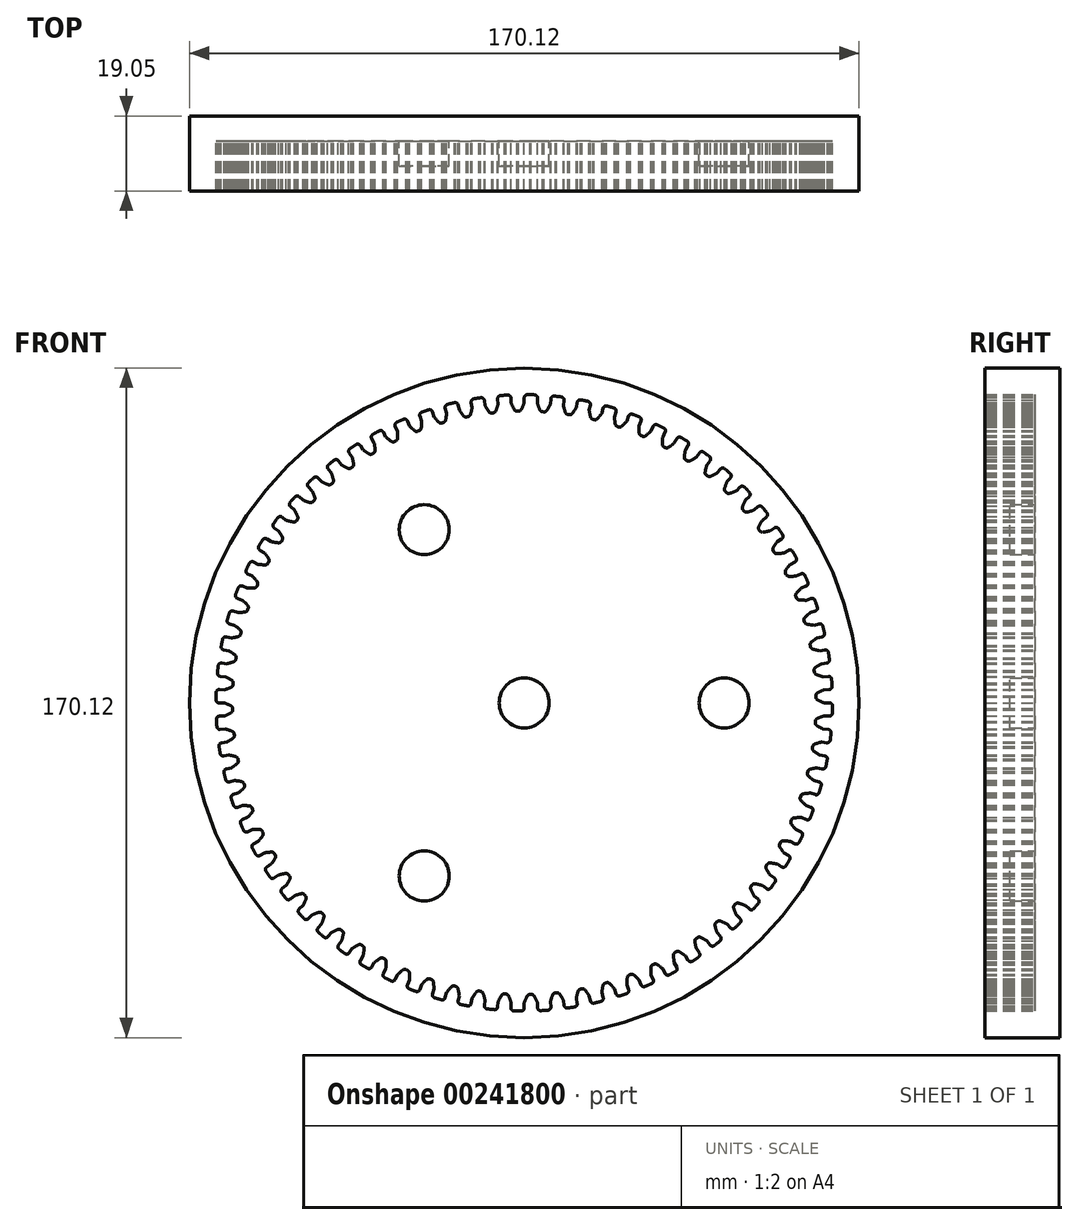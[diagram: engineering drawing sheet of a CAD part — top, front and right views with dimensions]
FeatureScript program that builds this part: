
annotation { "Feature Type Name" : "Feature", "Feature Type Description" : "" }
export const myFeature = defineFeature(function(context is Context, id is Id, definition is map)
    precondition{}
    {
        {
            var Q0;
            Q0=qCreatedBy(makeId("Front.planeOp"),FACE);
            var sketch = newSketch(context, id + "F0", { "sketchPlane" : qUnion([Q0])});
            skArc(sketch, "E0", {"start": v(-4.21, 78.2) * mm, "mid": v(-5.12, 78.15) * mm, "end": v(-6.03, 78.08) * mm});
            skLineSegment(sketch, "E1.MirrorCS", {"start": v(0, 76.2) * mm, "end": v(0, 77.53) * mm});
            skArc(sketch, "E2.MirrorCS", {"start": v(0, 76.2) * mm, "mid": v(-0.35, 75.36) * mm, "end": v(-0.73, 74.54) * mm});
            skArc(sketch, "E3.MirrorCS", {"start": v(-3.32, 76.13) * mm, "mid": v(-2.94, 75.3) * mm, "end": v(-2.52, 74.5) * mm});
            skLineSegment(sketch, "E4.MirrorCS", {"start": v(-3.32, 76.13) * mm, "end": v(-3.38, 77.45) * mm});
            skPoint(sketch, "E5.visualSharp", {"position": v(-2.27, 74.06) * mm});
            skArc(sketch, "E5.filletArc", {"start": v(-2.52, 74.5) * mm, "mid": v(-2.2, 74.19) * mm, "end": v(-1.78, 74.1) * mm});
            skPoint(sketch, "E6.visualSharp", {"position": v(-0.96, 74.09) * mm});
            skArc(sketch, "E6.filletArc", {"start": v(-1.45, 74.1) * mm, "mid": v(-1.03, 74.21) * mm, "end": v(-0.73, 74.54) * mm});
            skLineSegment(sketch, "E7", {"start": v(-1.78, 74.1) * mm, "end": v(-1.45, 74.1) * mm});
            skCircle(sketch, "E8", {"center": v(0, 0) * mm, "radius": 85.06 * mm});
            skPoint(sketch, "E9.visualSharp", {"position": v(-3.42, 78.24) * mm});
            skPoint(sketch, "E10.visualSharp", {"position": v(0, 78.32) * mm});
            skArc(sketch, "E11.filletArc", {"start": v(0.8, 78.31) * mm, "mid": v(0.23, 78.08) * mm, "end": v(0, 77.53) * mm});
            skArc(sketch, "E12.filletArc", {"start": v(-3.38, 77.45) * mm, "mid": v(-3.64, 78) * mm, "end": v(-4.21, 78.2) * mm});
            skArc(sketch, "E13.1.0", {"start": v(-10.12, 76.86) * mm, "mid": v(-10.42, 77.39) * mm, "end": v(-11.01, 77.54) * mm});
            skLineSegment(sketch, "E13.1.1", {"start": v(-9.95, 75.55) * mm, "end": v(-10.12, 76.86) * mm});
            skArc(sketch, "E13.1.2", {"start": v(-9.95, 75.55) * mm, "mid": v(-9.5, 74.76) * mm, "end": v(-9, 74) * mm});
            skArc(sketch, "E13.1.3", {"start": v(-9, 74) * mm, "mid": v(-8.66, 73.71) * mm, "end": v(-8.23, 73.66) * mm});
            skLineSegment(sketch, "E13.1.4", {"start": v(-8.23, 73.66) * mm, "end": v(-7.9, 73.7) * mm});
            skArc(sketch, "E13.1.5", {"start": v(-7.9, 73.7) * mm, "mid": v(-7.5, 73.84) * mm, "end": v(-7.23, 74.19) * mm});
            skArc(sketch, "E13.1.6", {"start": v(-6.64, 75.91) * mm, "mid": v(-6.91, 75.04) * mm, "end": v(-7.23, 74.19) * mm});
            skLineSegment(sketch, "E13.1.7", {"start": v(-6.64, 75.91) * mm, "end": v(-6.76, 77.23) * mm});
            skArc(sketch, "E13.1.8", {"start": v(-6.03, 78.08) * mm, "mid": v(-6.57, 77.8) * mm, "end": v(-6.76, 77.23) * mm});
            skArc(sketch, "E13.2.0", {"start": v(-16.78, 75.69) * mm, "mid": v(-17.13, 76.18) * mm, "end": v(-17.73, 76.28) * mm});
            skLineSegment(sketch, "E13.2.1", {"start": v(-16.5, 74.4) * mm, "end": v(-16.78, 75.69) * mm});
            skArc(sketch, "E13.2.2", {"start": v(-16.5, 74.4) * mm, "mid": v(-15.97, 73.65) * mm, "end": v(-15.42, 72.93) * mm});
            skArc(sketch, "E13.2.3", {"start": v(-15.42, 72.93) * mm, "mid": v(-15.06, 72.68) * mm, "end": v(-14.62, 72.66) * mm});
            skLineSegment(sketch, "E13.2.4", {"start": v(-14.62, 72.66) * mm, "end": v(-14.3, 72.72) * mm});
            skArc(sketch, "E13.2.5", {"start": v(-14.3, 72.72) * mm, "mid": v(-13.9, 72.9) * mm, "end": v(-13.66, 73.28) * mm});
            skArc(sketch, "E13.2.6", {"start": v(-13.23, 75.04) * mm, "mid": v(-13.43, 74.15) * mm, "end": v(-13.66, 73.28) * mm});
            skLineSegment(sketch, "E13.2.7", {"start": v(-13.23, 75.04) * mm, "end": v(-13.46, 76.35) * mm});
            skArc(sketch, "E13.2.8", {"start": v(-12.82, 77.26) * mm, "mid": v(-13.33, 76.94) * mm, "end": v(-13.46, 76.35) * mm});
            skArc(sketch, "E14.1.3.0", {"start": v(-23.31, 73.94) * mm, "mid": v(-23.7, 74.4) * mm, "end": v(-24.3, 74.45) * mm});
            skLineSegment(sketch, "E14.4.3.0", {"start": v(-22.91, 72.67) * mm, "end": v(-23.31, 73.94) * mm});
            skArc(sketch, "E14.7.3.0", {"start": v(-22.91, 72.67) * mm, "mid": v(-22.33, 71.98) * mm, "end": v(-21.71, 71.3) * mm});
            skArc(sketch, "E14.11.3.0", {"start": v(-21.71, 71.3) * mm, "mid": v(-21.33, 71.09) * mm, "end": v(-20.9, 71.1) * mm});
            skLineSegment(sketch, "E14.15.3.0", {"start": v(-20.9, 71.1) * mm, "end": v(-20.58, 71.2) * mm});
            skArc(sketch, "E14.18.3.0", {"start": v(-20.58, 71.2) * mm, "mid": v(-20.2, 71.42) * mm, "end": v(-20, 71.8) * mm});
            skArc(sketch, "E14.22.3.0", {"start": v(-19.72, 73.6) * mm, "mid": v(-19.84, 72.7) * mm, "end": v(-20, 71.8) * mm});
            skLineSegment(sketch, "E14.26.3.0", {"start": v(-19.72, 73.6) * mm, "end": v(-20.07, 74.88) * mm});
            skArc(sketch, "E14.29.3.0", {"start": v(-19.5, 75.85) * mm, "mid": v(-19.98, 75.48) * mm, "end": v(-20.07, 74.88) * mm});
            skArc(sketch, "E14.1.4.0", {"start": v(-29.67, 71.62) * mm, "mid": v(-30.1, 72.05) * mm, "end": v(-30.7, 72.05) * mm});
            skLineSegment(sketch, "E14.4.4.0", {"start": v(-29.16, 70.4) * mm, "end": v(-29.67, 71.62) * mm});
            skArc(sketch, "E14.7.4.0", {"start": v(-29.16, 70.4) * mm, "mid": v(-28.52, 69.76) * mm, "end": v(-27.85, 69.14) * mm});
            skArc(sketch, "E14.11.4.0", {"start": v(-27.85, 69.14) * mm, "mid": v(-27.45, 68.96) * mm, "end": v(-27.01, 69.02) * mm});
            skLineSegment(sketch, "E14.15.4.0", {"start": v(-27.01, 69.02) * mm, "end": v(-26.71, 69.13) * mm});
            skArc(sketch, "E14.18.4.0", {"start": v(-26.71, 69.13) * mm, "mid": v(-26.35, 69.39) * mm, "end": v(-26.18, 69.79) * mm});
            skArc(sketch, "E14.22.4.0", {"start": v(-26.06, 71.6) * mm, "mid": v(-26.1, 70.7) * mm, "end": v(-26.18, 69.79) * mm});
            skLineSegment(sketch, "E14.26.4.0", {"start": v(-26.06, 71.6) * mm, "end": v(-26.52, 72.85) * mm});
            skArc(sketch, "E14.29.4.0", {"start": v(-26.04, 73.86) * mm, "mid": v(-26.49, 73.46) * mm, "end": v(-26.52, 72.85) * mm});
            skArc(sketch, "E14.1.5.0", {"start": v(-35.8, 68.77) * mm, "mid": v(-36.26, 69.15) * mm, "end": v(-36.87, 69.1) * mm});
            skLineSegment(sketch, "E14.4.5.0", {"start": v(-35.19, 67.6) * mm, "end": v(-35.8, 68.77) * mm});
            skArc(sketch, "E14.7.5.0", {"start": v(-35.19, 67.6) * mm, "mid": v(-34.49, 67) * mm, "end": v(-33.77, 66.45) * mm});
            skArc(sketch, "E14.11.5.0", {"start": v(-33.77, 66.45) * mm, "mid": v(-33.35, 66.3) * mm, "end": v(-32.93, 66.4) * mm});
            skLineSegment(sketch, "E14.15.5.0", {"start": v(-32.93, 66.4) * mm, "end": v(-32.63, 66.54) * mm});
            skArc(sketch, "E14.18.5.0", {"start": v(-32.63, 66.54) * mm, "mid": v(-32.3, 66.82) * mm, "end": v(-32.16, 67.24) * mm});
            skArc(sketch, "E14.22.5.0", {"start": v(-32.2, 69.06) * mm, "mid": v(-32.16, 68.15) * mm, "end": v(-32.16, 67.24) * mm});
            skLineSegment(sketch, "E14.26.5.0", {"start": v(-32.2, 69.06) * mm, "end": v(-32.76, 70.26) * mm});
            skArc(sketch, "E14.29.5.0", {"start": v(-32.38, 71.31) * mm, "mid": v(-32.79, 70.87) * mm, "end": v(-32.76, 70.26) * mm});
            skArc(sketch, "E14.1.6.0", {"start": v(-41.65, 65.38) * mm, "mid": v(-42.15, 65.73) * mm, "end": v(-42.75, 65.62) * mm});
            skLineSegment(sketch, "E14.4.6.0", {"start": v(-40.94, 64.27) * mm, "end": v(-41.65, 65.38) * mm});
            skArc(sketch, "E14.7.6.0", {"start": v(-40.94, 64.27) * mm, "mid": v(-40.2, 63.74) * mm, "end": v(-39.43, 63.26) * mm});
            skArc(sketch, "E14.11.6.0", {"start": v(-39.43, 63.26) * mm, "mid": v(-39, 63.14) * mm, "end": v(-38.59, 63.28) * mm});
            skLineSegment(sketch, "E14.15.6.0", {"start": v(-38.59, 63.28) * mm, "end": v(-38.3, 63.45) * mm});
            skArc(sketch, "E14.18.6.0", {"start": v(-38.3, 63.45) * mm, "mid": v(-38, 63.76) * mm, "end": v(-37.9, 64.18) * mm});
            skArc(sketch, "E14.22.6.0", {"start": v(-38.1, 66) * mm, "mid": v(-37.98, 65.09) * mm, "end": v(-37.9, 64.18) * mm});
            skLineSegment(sketch, "E14.26.6.0", {"start": v(-38.1, 66) * mm, "end": v(-38.76, 67.14) * mm});
            skArc(sketch, "E14.29.6.0", {"start": v(-38.47, 68.22) * mm, "mid": v(-38.84, 67.74) * mm, "end": v(-38.76, 67.14) * mm});
            skArc(sketch, "E14.1.7.0", {"start": v(-47.2, 61.5) * mm, "mid": v(-47.72, 61.8) * mm, "end": v(-48.3, 61.65) * mm});
            skLineSegment(sketch, "E14.4.7.0", {"start": v(-46.39, 60.45) * mm, "end": v(-47.2, 61.5) * mm});
            skArc(sketch, "E14.7.7.0", {"start": v(-46.39, 60.45) * mm, "mid": v(-45.6, 60) * mm, "end": v(-44.8, 59.58) * mm});
            skArc(sketch, "E14.11.7.0", {"start": v(-44.8, 59.58) * mm, "mid": v(-44.36, 59.5) * mm, "end": v(-43.96, 59.67) * mm});
            skLineSegment(sketch, "E14.15.7.0", {"start": v(-43.96, 59.67) * mm, "end": v(-43.7, 59.86) * mm});
            skArc(sketch, "E14.18.7.0", {"start": v(-43.7, 59.86) * mm, "mid": v(-43.41, 60.2) * mm, "end": v(-43.35, 60.64) * mm});
            skArc(sketch, "E14.22.7.0", {"start": v(-43.7, 62.42) * mm, "mid": v(-43.5, 61.53) * mm, "end": v(-43.35, 60.64) * mm});
            skLineSegment(sketch, "E14.26.7.0", {"start": v(-43.7, 62.42) * mm, "end": v(-44.47, 63.5) * mm});
            skArc(sketch, "E14.29.7.0", {"start": v(-44.27, 64.6) * mm, "mid": v(-44.6, 64.1) * mm, "end": v(-44.47, 63.5) * mm});
            skArc(sketch, "E14.1.8.0", {"start": v(-52.38, 57.16) * mm, "mid": v(-52.93, 57.41) * mm, "end": v(-53.5, 57.2) * mm});
            skLineSegment(sketch, "E14.4.8.0", {"start": v(-51.48, 56.18) * mm, "end": v(-52.38, 57.16) * mm});
            skArc(sketch, "E14.7.8.0", {"start": v(-51.48, 56.18) * mm, "mid": v(-50.66, 55.8) * mm, "end": v(-49.82, 55.45) * mm});
            skArc(sketch, "E14.11.8.0", {"start": v(-49.82, 55.45) * mm, "mid": v(-49.38, 55.41) * mm, "end": v(-48.99, 55.62) * mm});
            skLineSegment(sketch, "E14.15.8.0", {"start": v(-48.99, 55.62) * mm, "end": v(-48.75, 55.83) * mm});
            skArc(sketch, "E14.18.8.0", {"start": v(-48.75, 55.83) * mm, "mid": v(-48.5, 56.19) * mm, "end": v(-48.47, 56.63) * mm});
            skArc(sketch, "E14.22.8.0", {"start": v(-48.98, 58.37) * mm, "mid": v(-48.7, 57.5) * mm, "end": v(-48.47, 56.63) * mm});
            skLineSegment(sketch, "E14.26.8.0", {"start": v(-48.98, 58.37) * mm, "end": v(-49.83, 59.39) * mm});
            skArc(sketch, "E14.29.8.0", {"start": v(-49.73, 60.5) * mm, "mid": v(-50.01, 59.97) * mm, "end": v(-49.83, 59.39) * mm});
            skArc(sketch, "E14.1.9.0", {"start": v(-57.16, 52.38) * mm, "mid": v(-57.73, 52.58) * mm, "end": v(-58.28, 52.32) * mm});
            skLineSegment(sketch, "E14.4.9.0", {"start": v(-56.18, 51.48) * mm, "end": v(-57.16, 52.38) * mm});
            skArc(sketch, "E14.7.9.0", {"start": v(-56.18, 51.48) * mm, "mid": v(-55.33, 51.17) * mm, "end": v(-54.46, 50.9) * mm});
            skArc(sketch, "E14.11.9.0", {"start": v(-54.46, 50.9) * mm, "mid": v(-54.02, 50.9) * mm, "end": v(-53.65, 51.13) * mm});
            skLineSegment(sketch, "E14.15.9.0", {"start": v(-53.65, 51.13) * mm, "end": v(-53.43, 51.37) * mm});
            skArc(sketch, "E14.18.9.0", {"start": v(-53.43, 51.37) * mm, "mid": v(-53.2, 51.75) * mm, "end": v(-53.22, 52.19) * mm});
            skArc(sketch, "E14.22.9.0", {"start": v(-53.88, 53.88) * mm, "mid": v(-53.53, 53.04) * mm, "end": v(-53.22, 52.19) * mm});
            skLineSegment(sketch, "E14.26.9.0", {"start": v(-53.88, 53.88) * mm, "end": v(-54.82, 54.82) * mm});
            skArc(sketch, "E14.29.9.0", {"start": v(-54.81, 55.94) * mm, "mid": v(-55.05, 55.38) * mm, "end": v(-54.82, 54.82) * mm});
            skArc(sketch, "E14.1.10.0", {"start": v(-61.5, 47.2) * mm, "mid": v(-62.1, 47.35) * mm, "end": v(-62.61, 47.04) * mm});
            skLineSegment(sketch, "E14.4.10.0", {"start": v(-60.45, 46.39) * mm, "end": v(-61.5, 47.2) * mm});
            skArc(sketch, "E14.7.10.0", {"start": v(-60.45, 46.39) * mm, "mid": v(-59.58, 46.15) * mm, "end": v(-58.69, 45.96) * mm});
            skArc(sketch, "E14.11.10.0", {"start": v(-58.69, 45.96) * mm, "mid": v(-58.25, 46) * mm, "end": v(-57.9, 46.26) * mm});
            skLineSegment(sketch, "E14.15.10.0", {"start": v(-57.9, 46.26) * mm, "end": v(-57.7, 46.52) * mm});
            skArc(sketch, "E14.18.10.0", {"start": v(-57.7, 46.52) * mm, "mid": v(-57.51, 46.91) * mm, "end": v(-57.57, 47.35) * mm});
            skArc(sketch, "E14.22.10.0", {"start": v(-58.37, 48.98) * mm, "mid": v(-57.95, 48.17) * mm, "end": v(-57.57, 47.35) * mm});
            skLineSegment(sketch, "E14.26.10.0", {"start": v(-58.37, 48.98) * mm, "end": v(-59.39, 49.83) * mm});
            skArc(sketch, "E14.29.10.0", {"start": v(-59.48, 50.95) * mm, "mid": v(-59.67, 50.37) * mm, "end": v(-59.39, 49.83) * mm});
            skArc(sketch, "E14.1.11.0", {"start": v(-65.38, 41.65) * mm, "mid": v(-65.98, 41.76) * mm, "end": v(-66.48, 41.4) * mm});
            skLineSegment(sketch, "E14.4.11.0", {"start": v(-64.27, 40.94) * mm, "end": v(-65.38, 41.65) * mm});
            skArc(sketch, "E14.7.11.0", {"start": v(-64.27, 40.94) * mm, "mid": v(-63.37, 40.78) * mm, "end": v(-62.47, 40.67) * mm});
            skArc(sketch, "E14.11.11.0", {"start": v(-62.47, 40.67) * mm, "mid": v(-62.04, 40.74) * mm, "end": v(-61.71, 41.04) * mm});
            skLineSegment(sketch, "E14.15.11.0", {"start": v(-61.71, 41.04) * mm, "end": v(-61.53, 41.31) * mm});
            skArc(sketch, "E14.18.11.0", {"start": v(-61.53, 41.31) * mm, "mid": v(-61.38, 41.72) * mm, "end": v(-61.48, 42.15) * mm});
            skArc(sketch, "E14.22.11.0", {"start": v(-62.42, 43.7) * mm, "mid": v(-61.93, 42.94) * mm, "end": v(-61.48, 42.15) * mm});
            skLineSegment(sketch, "E14.26.11.0", {"start": v(-62.42, 43.7) * mm, "end": v(-63.5, 44.47) * mm});
            skArc(sketch, "E14.29.11.0", {"start": v(-63.7, 45.57) * mm, "mid": v(-63.83, 44.98) * mm, "end": v(-63.5, 44.47) * mm});
            skArc(sketch, "E14.1.12.0", {"start": v(-68.77, 35.8) * mm, "mid": v(-69.37, 35.85) * mm, "end": v(-69.83, 35.46) * mm});
            skLineSegment(sketch, "E14.4.12.0", {"start": v(-67.6, 35.19) * mm, "end": v(-68.77, 35.8) * mm});
            skArc(sketch, "E14.7.12.0", {"start": v(-67.6, 35.19) * mm, "mid": v(-66.68, 35.1) * mm, "end": v(-65.78, 35.07) * mm});
            skArc(sketch, "E14.11.12.0", {"start": v(-65.78, 35.07) * mm, "mid": v(-65.35, 35.18) * mm, "end": v(-65.06, 35.5) * mm});
            skLineSegment(sketch, "E14.15.12.0", {"start": v(-65.06, 35.5) * mm, "end": v(-64.9, 35.8) * mm});
            skArc(sketch, "E14.18.12.0", {"start": v(-64.9, 35.8) * mm, "mid": v(-64.79, 36.21) * mm, "end": v(-64.92, 36.63) * mm});
            skArc(sketch, "E14.22.12.0", {"start": v(-66, 38.1) * mm, "mid": v(-65.44, 37.38) * mm, "end": v(-64.92, 36.63) * mm});
            skLineSegment(sketch, "E14.26.12.0", {"start": v(-66, 38.1) * mm, "end": v(-67.14, 38.76) * mm});
            skArc(sketch, "E14.29.12.0", {"start": v(-67.42, 39.85) * mm, "mid": v(-67.5, 39.24) * mm, "end": v(-67.14, 38.76) * mm});
            skArc(sketch, "E14.1.13.0", {"start": v(-71.62, 29.67) * mm, "mid": v(-72.23, 29.67) * mm, "end": v(-72.66, 29.23) * mm});
            skLineSegment(sketch, "E14.4.13.0", {"start": v(-70.4, 29.16) * mm, "end": v(-71.62, 29.67) * mm});
            skArc(sketch, "E14.7.13.0", {"start": v(-70.4, 29.16) * mm, "mid": v(-69.5, 29.16) * mm, "end": v(-68.58, 29.2) * mm});
            skArc(sketch, "E14.11.13.0", {"start": v(-68.58, 29.2) * mm, "mid": v(-68.17, 29.35) * mm, "end": v(-67.9, 29.7) * mm});
            skLineSegment(sketch, "E14.15.13.0", {"start": v(-67.9, 29.7) * mm, "end": v(-67.77, 30) * mm});
            skArc(sketch, "E14.18.13.0", {"start": v(-67.77, 30) * mm, "mid": v(-67.7, 30.43) * mm, "end": v(-67.86, 30.84) * mm});
            skArc(sketch, "E14.22.13.0", {"start": v(-69.06, 32.2) * mm, "mid": v(-68.45, 31.53) * mm, "end": v(-67.86, 30.84) * mm});
            skLineSegment(sketch, "E14.26.13.0", {"start": v(-69.06, 32.2) * mm, "end": v(-70.26, 32.76) * mm});
            skArc(sketch, "E14.29.13.0", {"start": v(-70.64, 33.82) * mm, "mid": v(-70.67, 33.21) * mm, "end": v(-70.26, 32.76) * mm});
            skArc(sketch, "E14.1.14.0", {"start": v(-73.94, 23.31) * mm, "mid": v(-74.54, 23.26) * mm, "end": v(-74.93, 22.8) * mm});
            skLineSegment(sketch, "E14.4.14.0", {"start": v(-72.67, 22.91) * mm, "end": v(-73.94, 23.31) * mm});
            skArc(sketch, "E14.7.14.0", {"start": v(-72.67, 22.91) * mm, "mid": v(-71.77, 23) * mm, "end": v(-70.87, 23.11) * mm});
            skArc(sketch, "E14.11.14.0", {"start": v(-70.87, 23.11) * mm, "mid": v(-70.47, 23.3) * mm, "end": v(-70.23, 23.67) * mm});
            skLineSegment(sketch, "E14.15.14.0", {"start": v(-70.23, 23.67) * mm, "end": v(-70.13, 23.98) * mm});
            skArc(sketch, "E14.18.14.0", {"start": v(-70.13, 23.98) * mm, "mid": v(-70.1, 24.41) * mm, "end": v(-70.3, 24.8) * mm});
            skArc(sketch, "E14.22.14.0", {"start": v(-71.6, 26.06) * mm, "mid": v(-70.93, 25.45) * mm, "end": v(-70.3, 24.8) * mm});
            skLineSegment(sketch, "E14.26.14.0", {"start": v(-71.6, 26.06) * mm, "end": v(-72.85, 26.52) * mm});
            skArc(sketch, "E14.29.14.0", {"start": v(-73.32, 27.53) * mm, "mid": v(-73.3, 26.93) * mm, "end": v(-72.85, 26.52) * mm});
            skArc(sketch, "E14.1.15.0", {"start": v(-75.69, 16.78) * mm, "mid": v(-76.28, 16.67) * mm, "end": v(-76.63, 16.17) * mm});
            skLineSegment(sketch, "E14.4.15.0", {"start": v(-74.4, 16.5) * mm, "end": v(-75.69, 16.78) * mm});
            skArc(sketch, "E14.7.15.0", {"start": v(-74.4, 16.5) * mm, "mid": v(-73.5, 16.65) * mm, "end": v(-72.61, 16.85) * mm});
            skArc(sketch, "E14.11.15.0", {"start": v(-72.61, 16.85) * mm, "mid": v(-72.23, 17.07) * mm, "end": v(-72.03, 17.46) * mm});
            skLineSegment(sketch, "E14.15.15.0", {"start": v(-72.03, 17.46) * mm, "end": v(-71.95, 17.77) * mm});
            skArc(sketch, "E14.18.15.0", {"start": v(-71.95, 17.77) * mm, "mid": v(-71.95, 18.21) * mm, "end": v(-72.19, 18.58) * mm});
            skArc(sketch, "E14.22.15.0", {"start": v(-73.6, 19.72) * mm, "mid": v(-72.88, 19.17) * mm, "end": v(-72.19, 18.58) * mm});
            skLineSegment(sketch, "E14.26.15.0", {"start": v(-73.6, 19.72) * mm, "end": v(-74.88, 20.07) * mm});
            skArc(sketch, "E14.29.15.0", {"start": v(-75.44, 21.04) * mm, "mid": v(-75.36, 20.44) * mm, "end": v(-74.88, 20.07) * mm});
            skArc(sketch, "E14.1.16.0", {"start": v(-76.86, 10.12) * mm, "mid": v(-77.45, 9.96) * mm, "end": v(-77.75, 9.43) * mm});
            skLineSegment(sketch, "E14.4.16.0", {"start": v(-75.55, 9.95) * mm, "end": v(-76.86, 10.12) * mm});
            skArc(sketch, "E14.7.16.0", {"start": v(-75.55, 9.95) * mm, "mid": v(-74.67, 10.18) * mm, "end": v(-73.8, 10.46) * mm});
            skArc(sketch, "E14.11.16.0", {"start": v(-73.8, 10.46) * mm, "mid": v(-73.44, 10.7) * mm, "end": v(-73.28, 11.11) * mm});
            skLineSegment(sketch, "E14.15.16.0", {"start": v(-73.28, 11.11) * mm, "end": v(-73.23, 11.43) * mm});
            skArc(sketch, "E14.18.16.0", {"start": v(-73.23, 11.43) * mm, "mid": v(-73.26, 11.87) * mm, "end": v(-73.53, 12.22) * mm});
            skArc(sketch, "E14.22.16.0", {"start": v(-75.04, 13.23) * mm, "mid": v(-74.27, 12.74) * mm, "end": v(-73.53, 12.22) * mm});
            skLineSegment(sketch, "E14.26.16.0", {"start": v(-75.04, 13.23) * mm, "end": v(-76.35, 13.46) * mm});
            skArc(sketch, "E14.29.16.0", {"start": v(-76.98, 14.38) * mm, "mid": v(-76.86, 13.79) * mm, "end": v(-76.35, 13.46) * mm});
            skArc(sketch, "E14.1.17.0", {"start": v(-77.45, 3.38) * mm, "mid": v(-78.02, 3.17) * mm, "end": v(-78.27, 2.62) * mm});
            skLineSegment(sketch, "E14.4.17.0", {"start": v(-76.13, 3.32) * mm, "end": v(-77.45, 3.38) * mm});
            skArc(sketch, "E14.7.17.0", {"start": v(-76.13, 3.32) * mm, "mid": v(-75.27, 3.63) * mm, "end": v(-74.43, 3.98) * mm});
            skArc(sketch, "E14.11.17.0", {"start": v(-74.43, 3.98) * mm, "mid": v(-74.1, 4.27) * mm, "end": v(-73.97, 4.69) * mm});
            skLineSegment(sketch, "E14.15.17.0", {"start": v(-73.97, 4.69) * mm, "end": v(-73.94, 5) * mm});
            skArc(sketch, "E14.18.17.0", {"start": v(-73.94, 5) * mm, "mid": v(-74.02, 5.44) * mm, "end": v(-74.32, 5.77) * mm});
            skArc(sketch, "E14.22.17.0", {"start": v(-75.91, 6.64) * mm, "mid": v(-75.1, 6.22) * mm, "end": v(-74.32, 5.77) * mm});
            skLineSegment(sketch, "E14.26.17.0", {"start": v(-75.91, 6.64) * mm, "end": v(-77.23, 6.76) * mm});
            skArc(sketch, "E14.29.17.0", {"start": v(-77.95, 7.62) * mm, "mid": v(-77.77, 7.04) * mm, "end": v(-77.23, 6.76) * mm});
            skArc(sketch, "E14.1.18.0", {"start": v(-77.45, -3.38) * mm, "mid": v(-78, -3.64) * mm, "end": v(-78.2, -4.21) * mm});
            skLineSegment(sketch, "E14.4.18.0", {"start": v(-76.13, -3.32) * mm, "end": v(-77.45, -3.38) * mm});
            skArc(sketch, "E14.7.18.0", {"start": v(-76.13, -3.32) * mm, "mid": v(-75.3, -2.94) * mm, "end": v(-74.5, -2.52) * mm});
            skArc(sketch, "E14.11.18.0", {"start": v(-74.5, -2.52) * mm, "mid": v(-74.19, -2.2) * mm, "end": v(-74.1, -1.78) * mm});
            skLineSegment(sketch, "E14.15.18.0", {"start": v(-74.1, -1.78) * mm, "end": v(-74.1, -1.45) * mm});
            skArc(sketch, "E14.18.18.0", {"start": v(-74.1, -1.45) * mm, "mid": v(-74.21, -1.03) * mm, "end": v(-74.54, -0.73) * mm});
            skArc(sketch, "E14.22.18.0", {"start": v(-76.2, 0) * mm, "mid": v(-75.36, -0.35) * mm, "end": v(-74.54, -0.73) * mm});
            skLineSegment(sketch, "E14.26.18.0", {"start": v(-76.2, 0) * mm, "end": v(-77.53, 0) * mm});
            skArc(sketch, "E14.29.18.0", {"start": v(-78.31, 0.8) * mm, "mid": v(-78.08, 0.23) * mm, "end": v(-77.53, 0) * mm});
            skArc(sketch, "E14.1.19.0", {"start": v(-76.86, -10.12) * mm, "mid": v(-77.39, -10.42) * mm, "end": v(-77.54, -11.01) * mm});
            skLineSegment(sketch, "E14.4.19.0", {"start": v(-75.55, -9.95) * mm, "end": v(-76.86, -10.12) * mm});
            skArc(sketch, "E14.7.19.0", {"start": v(-75.55, -9.95) * mm, "mid": v(-74.76, -9.5) * mm, "end": v(-74, -9) * mm});
            skArc(sketch, "E14.11.19.0", {"start": v(-74, -9) * mm, "mid": v(-73.71, -8.66) * mm, "end": v(-73.66, -8.23) * mm});
            skLineSegment(sketch, "E14.15.19.0", {"start": v(-73.66, -8.23) * mm, "end": v(-73.7, -7.9) * mm});
            skArc(sketch, "E14.18.19.0", {"start": v(-73.7, -7.9) * mm, "mid": v(-73.84, -7.5) * mm, "end": v(-74.19, -7.23) * mm});
            skArc(sketch, "E14.22.19.0", {"start": v(-75.91, -6.64) * mm, "mid": v(-75.04, -6.91) * mm, "end": v(-74.19, -7.23) * mm});
            skLineSegment(sketch, "E14.26.19.0", {"start": v(-75.91, -6.64) * mm, "end": v(-77.23, -6.76) * mm});
            skArc(sketch, "E14.29.19.0", {"start": v(-78.08, -6.03) * mm, "mid": v(-77.8, -6.57) * mm, "end": v(-77.23, -6.76) * mm});
            skArc(sketch, "E14.1.20.0", {"start": v(-75.69, -16.78) * mm, "mid": v(-76.18, -17.13) * mm, "end": v(-76.28, -17.73) * mm});
            skLineSegment(sketch, "E14.4.20.0", {"start": v(-74.4, -16.5) * mm, "end": v(-75.69, -16.78) * mm});
            skArc(sketch, "E14.7.20.0", {"start": v(-74.4, -16.5) * mm, "mid": v(-73.65, -15.97) * mm, "end": v(-72.93, -15.42) * mm});
            skArc(sketch, "E14.11.20.0", {"start": v(-72.93, -15.42) * mm, "mid": v(-72.68, -15.06) * mm, "end": v(-72.66, -14.62) * mm});
            skLineSegment(sketch, "E14.15.20.0", {"start": v(-72.66, -14.62) * mm, "end": v(-72.72, -14.3) * mm});
            skArc(sketch, "E14.18.20.0", {"start": v(-72.72, -14.3) * mm, "mid": v(-72.9, -13.9) * mm, "end": v(-73.28, -13.66) * mm});
            skArc(sketch, "E14.22.20.0", {"start": v(-75.04, -13.23) * mm, "mid": v(-74.15, -13.43) * mm, "end": v(-73.28, -13.66) * mm});
            skLineSegment(sketch, "E14.26.20.0", {"start": v(-75.04, -13.23) * mm, "end": v(-76.35, -13.46) * mm});
            skArc(sketch, "E14.29.20.0", {"start": v(-77.26, -12.82) * mm, "mid": v(-76.94, -13.33) * mm, "end": v(-76.35, -13.46) * mm});
            skArc(sketch, "E14.1.21.0", {"start": v(-73.94, -23.31) * mm, "mid": v(-74.4, -23.7) * mm, "end": v(-74.45, -24.3) * mm});
            skLineSegment(sketch, "E14.4.21.0", {"start": v(-72.67, -22.91) * mm, "end": v(-73.94, -23.31) * mm});
            skArc(sketch, "E14.7.21.0", {"start": v(-72.67, -22.91) * mm, "mid": v(-71.98, -22.33) * mm, "end": v(-71.3, -21.71) * mm});
            skArc(sketch, "E14.11.21.0", {"start": v(-71.3, -21.71) * mm, "mid": v(-71.09, -21.33) * mm, "end": v(-71.1, -20.9) * mm});
            skLineSegment(sketch, "E14.15.21.0", {"start": v(-71.1, -20.9) * mm, "end": v(-71.2, -20.58) * mm});
            skArc(sketch, "E14.18.21.0", {"start": v(-71.2, -20.58) * mm, "mid": v(-71.42, -20.2) * mm, "end": v(-71.8, -20) * mm});
            skArc(sketch, "E14.22.21.0", {"start": v(-73.6, -19.72) * mm, "mid": v(-72.7, -19.84) * mm, "end": v(-71.8, -20) * mm});
            skLineSegment(sketch, "E14.26.21.0", {"start": v(-73.6, -19.72) * mm, "end": v(-74.88, -20.07) * mm});
            skArc(sketch, "E14.29.21.0", {"start": v(-75.85, -19.5) * mm, "mid": v(-75.48, -19.98) * mm, "end": v(-74.88, -20.07) * mm});
            skArc(sketch, "E14.1.22.0", {"start": v(-71.62, -29.67) * mm, "mid": v(-72.05, -30.1) * mm, "end": v(-72.05, -30.7) * mm});
            skLineSegment(sketch, "E14.4.22.0", {"start": v(-70.4, -29.16) * mm, "end": v(-71.62, -29.67) * mm});
            skArc(sketch, "E14.7.22.0", {"start": v(-70.4, -29.16) * mm, "mid": v(-69.76, -28.52) * mm, "end": v(-69.14, -27.85) * mm});
            skArc(sketch, "E14.11.22.0", {"start": v(-69.14, -27.85) * mm, "mid": v(-68.96, -27.45) * mm, "end": v(-69.02, -27.01) * mm});
            skLineSegment(sketch, "E14.15.22.0", {"start": v(-69.02, -27.01) * mm, "end": v(-69.13, -26.71) * mm});
            skArc(sketch, "E14.18.22.0", {"start": v(-69.13, -26.71) * mm, "mid": v(-69.39, -26.35) * mm, "end": v(-69.79, -26.18) * mm});
            skArc(sketch, "E14.22.22.0", {"start": v(-71.6, -26.06) * mm, "mid": v(-70.7, -26.1) * mm, "end": v(-69.79, -26.18) * mm});
            skLineSegment(sketch, "E14.26.22.0", {"start": v(-71.6, -26.06) * mm, "end": v(-72.85, -26.52) * mm});
            skArc(sketch, "E14.29.22.0", {"start": v(-73.86, -26.04) * mm, "mid": v(-73.46, -26.49) * mm, "end": v(-72.85, -26.52) * mm});
            skArc(sketch, "E14.1.23.0", {"start": v(-68.77, -35.8) * mm, "mid": v(-69.15, -36.26) * mm, "end": v(-69.1, -36.87) * mm});
            skLineSegment(sketch, "E14.4.23.0", {"start": v(-67.6, -35.19) * mm, "end": v(-68.77, -35.8) * mm});
            skArc(sketch, "E14.7.23.0", {"start": v(-67.6, -35.19) * mm, "mid": v(-67, -34.49) * mm, "end": v(-66.45, -33.77) * mm});
            skArc(sketch, "E14.11.23.0", {"start": v(-66.45, -33.77) * mm, "mid": v(-66.3, -33.35) * mm, "end": v(-66.4, -32.93) * mm});
            skLineSegment(sketch, "E14.15.23.0", {"start": v(-66.4, -32.93) * mm, "end": v(-66.54, -32.63) * mm});
            skArc(sketch, "E14.18.23.0", {"start": v(-66.54, -32.63) * mm, "mid": v(-66.82, -32.3) * mm, "end": v(-67.24, -32.16) * mm});
            skArc(sketch, "E14.22.23.0", {"start": v(-69.06, -32.2) * mm, "mid": v(-68.15, -32.16) * mm, "end": v(-67.24, -32.16) * mm});
            skLineSegment(sketch, "E14.26.23.0", {"start": v(-69.06, -32.2) * mm, "end": v(-70.26, -32.76) * mm});
            skArc(sketch, "E14.29.23.0", {"start": v(-71.31, -32.38) * mm, "mid": v(-70.87, -32.79) * mm, "end": v(-70.26, -32.76) * mm});
            skArc(sketch, "E14.1.24.0", {"start": v(-65.38, -41.65) * mm, "mid": v(-65.73, -42.15) * mm, "end": v(-65.62, -42.75) * mm});
            skLineSegment(sketch, "E14.4.24.0", {"start": v(-64.27, -40.94) * mm, "end": v(-65.38, -41.65) * mm});
            skArc(sketch, "E14.7.24.0", {"start": v(-64.27, -40.94) * mm, "mid": v(-63.74, -40.2) * mm, "end": v(-63.26, -39.43) * mm});
            skArc(sketch, "E14.11.24.0", {"start": v(-63.26, -39.43) * mm, "mid": v(-63.14, -39) * mm, "end": v(-63.28, -38.59) * mm});
            skLineSegment(sketch, "E14.15.24.0", {"start": v(-63.28, -38.59) * mm, "end": v(-63.45, -38.3) * mm});
            skArc(sketch, "E14.18.24.0", {"start": v(-63.45, -38.3) * mm, "mid": v(-63.76, -38) * mm, "end": v(-64.18, -37.9) * mm});
            skArc(sketch, "E14.22.24.0", {"start": v(-66, -38.1) * mm, "mid": v(-65.09, -37.98) * mm, "end": v(-64.18, -37.9) * mm});
            skLineSegment(sketch, "E14.26.24.0", {"start": v(-66, -38.1) * mm, "end": v(-67.14, -38.76) * mm});
            skArc(sketch, "E14.29.24.0", {"start": v(-68.22, -38.47) * mm, "mid": v(-67.74, -38.84) * mm, "end": v(-67.14, -38.76) * mm});
            skArc(sketch, "E14.1.25.0", {"start": v(-61.5, -47.2) * mm, "mid": v(-61.8, -47.72) * mm, "end": v(-61.65, -48.3) * mm});
            skLineSegment(sketch, "E14.4.25.0", {"start": v(-60.45, -46.39) * mm, "end": v(-61.5, -47.2) * mm});
            skArc(sketch, "E14.7.25.0", {"start": v(-60.45, -46.39) * mm, "mid": v(-60, -45.6) * mm, "end": v(-59.58, -44.8) * mm});
            skArc(sketch, "E14.11.25.0", {"start": v(-59.58, -44.8) * mm, "mid": v(-59.5, -44.36) * mm, "end": v(-59.67, -43.96) * mm});
            skLineSegment(sketch, "E14.15.25.0", {"start": v(-59.67, -43.96) * mm, "end": v(-59.86, -43.7) * mm});
            skArc(sketch, "E14.18.25.0", {"start": v(-59.86, -43.7) * mm, "mid": v(-60.2, -43.41) * mm, "end": v(-60.64, -43.35) * mm});
            skArc(sketch, "E14.22.25.0", {"start": v(-62.42, -43.7) * mm, "mid": v(-61.53, -43.5) * mm, "end": v(-60.64, -43.35) * mm});
            skLineSegment(sketch, "E14.26.25.0", {"start": v(-62.42, -43.7) * mm, "end": v(-63.5, -44.47) * mm});
            skArc(sketch, "E14.29.25.0", {"start": v(-64.6, -44.27) * mm, "mid": v(-64.1, -44.6) * mm, "end": v(-63.5, -44.47) * mm});
            skArc(sketch, "E14.1.26.0", {"start": v(-57.16, -52.38) * mm, "mid": v(-57.41, -52.93) * mm, "end": v(-57.2, -53.5) * mm});
            skLineSegment(sketch, "E14.4.26.0", {"start": v(-56.18, -51.48) * mm, "end": v(-57.16, -52.38) * mm});
            skArc(sketch, "E14.7.26.0", {"start": v(-56.18, -51.48) * mm, "mid": v(-55.8, -50.66) * mm, "end": v(-55.45, -49.82) * mm});
            skArc(sketch, "E14.11.26.0", {"start": v(-55.45, -49.82) * mm, "mid": v(-55.41, -49.38) * mm, "end": v(-55.62, -48.99) * mm});
            skLineSegment(sketch, "E14.15.26.0", {"start": v(-55.62, -48.99) * mm, "end": v(-55.83, -48.75) * mm});
            skArc(sketch, "E14.18.26.0", {"start": v(-55.83, -48.75) * mm, "mid": v(-56.19, -48.5) * mm, "end": v(-56.63, -48.47) * mm});
            skArc(sketch, "E14.22.26.0", {"start": v(-58.37, -48.98) * mm, "mid": v(-57.5, -48.7) * mm, "end": v(-56.63, -48.47) * mm});
            skLineSegment(sketch, "E14.26.26.0", {"start": v(-58.37, -48.98) * mm, "end": v(-59.39, -49.83) * mm});
            skArc(sketch, "E14.29.26.0", {"start": v(-60.5, -49.73) * mm, "mid": v(-59.97, -50.01) * mm, "end": v(-59.39, -49.83) * mm});
            skArc(sketch, "E14.1.27.0", {"start": v(-52.38, -57.16) * mm, "mid": v(-52.58, -57.73) * mm, "end": v(-52.32, -58.28) * mm});
            skLineSegment(sketch, "E14.4.27.0", {"start": v(-51.48, -56.18) * mm, "end": v(-52.38, -57.16) * mm});
            skArc(sketch, "E14.7.27.0", {"start": v(-51.48, -56.18) * mm, "mid": v(-51.17, -55.33) * mm, "end": v(-50.9, -54.46) * mm});
            skArc(sketch, "E14.11.27.0", {"start": v(-50.9, -54.46) * mm, "mid": v(-50.9, -54.02) * mm, "end": v(-51.13, -53.65) * mm});
            skLineSegment(sketch, "E14.15.27.0", {"start": v(-51.13, -53.65) * mm, "end": v(-51.37, -53.43) * mm});
            skArc(sketch, "E14.18.27.0", {"start": v(-51.37, -53.43) * mm, "mid": v(-51.75, -53.2) * mm, "end": v(-52.19, -53.22) * mm});
            skArc(sketch, "E14.22.27.0", {"start": v(-53.88, -53.88) * mm, "mid": v(-53.04, -53.53) * mm, "end": v(-52.19, -53.22) * mm});
            skLineSegment(sketch, "E14.26.27.0", {"start": v(-53.88, -53.88) * mm, "end": v(-54.82, -54.82) * mm});
            skArc(sketch, "E14.29.27.0", {"start": v(-55.94, -54.81) * mm, "mid": v(-55.38, -55.05) * mm, "end": v(-54.82, -54.82) * mm});
            skArc(sketch, "E14.1.28.0", {"start": v(-47.2, -61.5) * mm, "mid": v(-47.35, -62.1) * mm, "end": v(-47.04, -62.61) * mm});
            skLineSegment(sketch, "E14.4.28.0", {"start": v(-46.39, -60.45) * mm, "end": v(-47.2, -61.5) * mm});
            skArc(sketch, "E14.7.28.0", {"start": v(-46.39, -60.45) * mm, "mid": v(-46.15, -59.58) * mm, "end": v(-45.96, -58.69) * mm});
            skArc(sketch, "E14.11.28.0", {"start": v(-45.96, -58.69) * mm, "mid": v(-46, -58.25) * mm, "end": v(-46.26, -57.9) * mm});
            skLineSegment(sketch, "E14.15.28.0", {"start": v(-46.26, -57.9) * mm, "end": v(-46.52, -57.7) * mm});
            skArc(sketch, "E14.18.28.0", {"start": v(-46.52, -57.7) * mm, "mid": v(-46.91, -57.51) * mm, "end": v(-47.35, -57.57) * mm});
            skArc(sketch, "E14.22.28.0", {"start": v(-48.98, -58.37) * mm, "mid": v(-48.17, -57.95) * mm, "end": v(-47.35, -57.57) * mm});
            skLineSegment(sketch, "E14.26.28.0", {"start": v(-48.98, -58.37) * mm, "end": v(-49.83, -59.39) * mm});
            skArc(sketch, "E14.29.28.0", {"start": v(-50.95, -59.48) * mm, "mid": v(-50.37, -59.67) * mm, "end": v(-49.83, -59.39) * mm});
            skArc(sketch, "E14.1.29.0", {"start": v(-41.65, -65.38) * mm, "mid": v(-41.76, -65.98) * mm, "end": v(-41.4, -66.48) * mm});
            skLineSegment(sketch, "E14.4.29.0", {"start": v(-40.94, -64.27) * mm, "end": v(-41.65, -65.38) * mm});
            skArc(sketch, "E14.7.29.0", {"start": v(-40.94, -64.27) * mm, "mid": v(-40.78, -63.37) * mm, "end": v(-40.67, -62.47) * mm});
            skArc(sketch, "E14.11.29.0", {"start": v(-40.67, -62.47) * mm, "mid": v(-40.74, -62.04) * mm, "end": v(-41.04, -61.71) * mm});
            skLineSegment(sketch, "E14.15.29.0", {"start": v(-41.04, -61.71) * mm, "end": v(-41.31, -61.53) * mm});
            skArc(sketch, "E14.18.29.0", {"start": v(-41.31, -61.53) * mm, "mid": v(-41.72, -61.38) * mm, "end": v(-42.15, -61.48) * mm});
            skArc(sketch, "E14.22.29.0", {"start": v(-43.7, -62.42) * mm, "mid": v(-42.94, -61.93) * mm, "end": v(-42.15, -61.48) * mm});
            skLineSegment(sketch, "E14.26.29.0", {"start": v(-43.7, -62.42) * mm, "end": v(-44.47, -63.5) * mm});
            skArc(sketch, "E14.29.29.0", {"start": v(-45.57, -63.7) * mm, "mid": v(-44.98, -63.83) * mm, "end": v(-44.47, -63.5) * mm});
            skArc(sketch, "E14.1.30.0", {"start": v(-35.8, -68.77) * mm, "mid": v(-35.85, -69.37) * mm, "end": v(-35.46, -69.83) * mm});
            skLineSegment(sketch, "E14.4.30.0", {"start": v(-35.19, -67.6) * mm, "end": v(-35.8, -68.77) * mm});
            skArc(sketch, "E14.7.30.0", {"start": v(-35.19, -67.6) * mm, "mid": v(-35.1, -66.68) * mm, "end": v(-35.07, -65.78) * mm});
            skArc(sketch, "E14.11.30.0", {"start": v(-35.07, -65.78) * mm, "mid": v(-35.18, -65.35) * mm, "end": v(-35.5, -65.06) * mm});
            skLineSegment(sketch, "E14.15.30.0", {"start": v(-35.5, -65.06) * mm, "end": v(-35.8, -64.9) * mm});
            skArc(sketch, "E14.18.30.0", {"start": v(-35.8, -64.9) * mm, "mid": v(-36.21, -64.79) * mm, "end": v(-36.63, -64.92) * mm});
            skArc(sketch, "E14.22.30.0", {"start": v(-38.1, -66) * mm, "mid": v(-37.38, -65.44) * mm, "end": v(-36.63, -64.92) * mm});
            skLineSegment(sketch, "E14.26.30.0", {"start": v(-38.1, -66) * mm, "end": v(-38.76, -67.14) * mm});
            skArc(sketch, "E14.29.30.0", {"start": v(-39.85, -67.42) * mm, "mid": v(-39.24, -67.5) * mm, "end": v(-38.76, -67.14) * mm});
            skArc(sketch, "E14.1.31.0", {"start": v(-29.67, -71.62) * mm, "mid": v(-29.67, -72.23) * mm, "end": v(-29.23, -72.66) * mm});
            skLineSegment(sketch, "E14.4.31.0", {"start": v(-29.16, -70.4) * mm, "end": v(-29.67, -71.62) * mm});
            skArc(sketch, "E14.7.31.0", {"start": v(-29.16, -70.4) * mm, "mid": v(-29.16, -69.5) * mm, "end": v(-29.2, -68.58) * mm});
            skArc(sketch, "E14.11.31.0", {"start": v(-29.2, -68.58) * mm, "mid": v(-29.35, -68.17) * mm, "end": v(-29.7, -67.9) * mm});
            skLineSegment(sketch, "E14.15.31.0", {"start": v(-29.7, -67.9) * mm, "end": v(-30, -67.77) * mm});
            skArc(sketch, "E14.18.31.0", {"start": v(-30, -67.77) * mm, "mid": v(-30.43, -67.7) * mm, "end": v(-30.84, -67.86) * mm});
            skArc(sketch, "E14.22.31.0", {"start": v(-32.2, -69.06) * mm, "mid": v(-31.53, -68.45) * mm, "end": v(-30.84, -67.86) * mm});
            skLineSegment(sketch, "E14.26.31.0", {"start": v(-32.2, -69.06) * mm, "end": v(-32.76, -70.26) * mm});
            skArc(sketch, "E14.29.31.0", {"start": v(-33.82, -70.64) * mm, "mid": v(-33.21, -70.67) * mm, "end": v(-32.76, -70.26) * mm});
            skArc(sketch, "E14.1.32.0", {"start": v(-23.31, -73.94) * mm, "mid": v(-23.26, -74.54) * mm, "end": v(-22.8, -74.93) * mm});
            skLineSegment(sketch, "E14.4.32.0", {"start": v(-22.91, -72.67) * mm, "end": v(-23.31, -73.94) * mm});
            skArc(sketch, "E14.7.32.0", {"start": v(-22.91, -72.67) * mm, "mid": v(-23, -71.77) * mm, "end": v(-23.11, -70.87) * mm});
            skArc(sketch, "E14.11.32.0", {"start": v(-23.11, -70.87) * mm, "mid": v(-23.3, -70.47) * mm, "end": v(-23.67, -70.23) * mm});
            skLineSegment(sketch, "E14.15.32.0", {"start": v(-23.67, -70.23) * mm, "end": v(-23.98, -70.13) * mm});
            skArc(sketch, "E14.18.32.0", {"start": v(-23.98, -70.13) * mm, "mid": v(-24.41, -70.1) * mm, "end": v(-24.8, -70.3) * mm});
            skArc(sketch, "E14.22.32.0", {"start": v(-26.06, -71.6) * mm, "mid": v(-25.45, -70.93) * mm, "end": v(-24.8, -70.3) * mm});
            skLineSegment(sketch, "E14.26.32.0", {"start": v(-26.06, -71.6) * mm, "end": v(-26.52, -72.85) * mm});
            skArc(sketch, "E14.29.32.0", {"start": v(-27.53, -73.32) * mm, "mid": v(-26.93, -73.3) * mm, "end": v(-26.52, -72.85) * mm});
            skArc(sketch, "E14.1.33.0", {"start": v(-16.78, -75.69) * mm, "mid": v(-16.67, -76.28) * mm, "end": v(-16.17, -76.63) * mm});
            skLineSegment(sketch, "E14.4.33.0", {"start": v(-16.5, -74.4) * mm, "end": v(-16.78, -75.69) * mm});
            skArc(sketch, "E14.7.33.0", {"start": v(-16.5, -74.4) * mm, "mid": v(-16.65, -73.5) * mm, "end": v(-16.85, -72.61) * mm});
            skArc(sketch, "E14.11.33.0", {"start": v(-16.85, -72.61) * mm, "mid": v(-17.07, -72.23) * mm, "end": v(-17.46, -72.03) * mm});
            skLineSegment(sketch, "E14.15.33.0", {"start": v(-17.46, -72.03) * mm, "end": v(-17.77, -71.95) * mm});
            skArc(sketch, "E14.18.33.0", {"start": v(-17.77, -71.95) * mm, "mid": v(-18.21, -71.95) * mm, "end": v(-18.58, -72.19) * mm});
            skArc(sketch, "E14.22.33.0", {"start": v(-19.72, -73.6) * mm, "mid": v(-19.17, -72.88) * mm, "end": v(-18.58, -72.19) * mm});
            skLineSegment(sketch, "E14.26.33.0", {"start": v(-19.72, -73.6) * mm, "end": v(-20.07, -74.88) * mm});
            skArc(sketch, "E14.29.33.0", {"start": v(-21.04, -75.44) * mm, "mid": v(-20.44, -75.36) * mm, "end": v(-20.07, -74.88) * mm});
            skArc(sketch, "E14.1.34.0", {"start": v(-10.12, -76.86) * mm, "mid": v(-9.96, -77.45) * mm, "end": v(-9.43, -77.75) * mm});
            skLineSegment(sketch, "E14.4.34.0", {"start": v(-9.95, -75.55) * mm, "end": v(-10.12, -76.86) * mm});
            skArc(sketch, "E14.7.34.0", {"start": v(-9.95, -75.55) * mm, "mid": v(-10.18, -74.67) * mm, "end": v(-10.46, -73.8) * mm});
            skArc(sketch, "E14.11.34.0", {"start": v(-10.46, -73.8) * mm, "mid": v(-10.7, -73.44) * mm, "end": v(-11.11, -73.28) * mm});
            skLineSegment(sketch, "E14.15.34.0", {"start": v(-11.11, -73.28) * mm, "end": v(-11.43, -73.23) * mm});
            skArc(sketch, "E14.18.34.0", {"start": v(-11.43, -73.23) * mm, "mid": v(-11.87, -73.26) * mm, "end": v(-12.22, -73.53) * mm});
            skArc(sketch, "E14.22.34.0", {"start": v(-13.23, -75.04) * mm, "mid": v(-12.74, -74.27) * mm, "end": v(-12.22, -73.53) * mm});
            skLineSegment(sketch, "E14.26.34.0", {"start": v(-13.23, -75.04) * mm, "end": v(-13.46, -76.35) * mm});
            skArc(sketch, "E14.29.34.0", {"start": v(-14.38, -76.98) * mm, "mid": v(-13.79, -76.86) * mm, "end": v(-13.46, -76.35) * mm});
            skArc(sketch, "E14.1.35.0", {"start": v(-3.38, -77.45) * mm, "mid": v(-3.17, -78.02) * mm, "end": v(-2.62, -78.27) * mm});
            skLineSegment(sketch, "E14.4.35.0", {"start": v(-3.32, -76.13) * mm, "end": v(-3.38, -77.45) * mm});
            skArc(sketch, "E14.7.35.0", {"start": v(-3.32, -76.13) * mm, "mid": v(-3.63, -75.27) * mm, "end": v(-3.98, -74.43) * mm});
            skArc(sketch, "E14.11.35.0", {"start": v(-3.98, -74.43) * mm, "mid": v(-4.27, -74.1) * mm, "end": v(-4.69, -73.97) * mm});
            skLineSegment(sketch, "E14.15.35.0", {"start": v(-4.69, -73.97) * mm, "end": v(-5, -73.94) * mm});
            skArc(sketch, "E14.18.35.0", {"start": v(-5, -73.94) * mm, "mid": v(-5.44, -74.02) * mm, "end": v(-5.77, -74.32) * mm});
            skArc(sketch, "E14.22.35.0", {"start": v(-6.64, -75.91) * mm, "mid": v(-6.22, -75.1) * mm, "end": v(-5.77, -74.32) * mm});
            skLineSegment(sketch, "E14.26.35.0", {"start": v(-6.64, -75.91) * mm, "end": v(-6.76, -77.23) * mm});
            skArc(sketch, "E14.29.35.0", {"start": v(-7.62, -77.95) * mm, "mid": v(-7.04, -77.77) * mm, "end": v(-6.76, -77.23) * mm});
            skArc(sketch, "E14.1.36.0", {"start": v(3.38, -77.45) * mm, "mid": v(3.64, -78) * mm, "end": v(4.21, -78.2) * mm});
            skLineSegment(sketch, "E14.4.36.0", {"start": v(3.32, -76.13) * mm, "end": v(3.38, -77.45) * mm});
            skArc(sketch, "E14.7.36.0", {"start": v(3.32, -76.13) * mm, "mid": v(2.94, -75.3) * mm, "end": v(2.52, -74.5) * mm});
            skArc(sketch, "E14.11.36.0", {"start": v(2.52, -74.5) * mm, "mid": v(2.2, -74.19) * mm, "end": v(1.78, -74.1) * mm});
            skLineSegment(sketch, "E14.15.36.0", {"start": v(1.78, -74.1) * mm, "end": v(1.45, -74.1) * mm});
            skArc(sketch, "E14.18.36.0", {"start": v(1.45, -74.1) * mm, "mid": v(1.03, -74.21) * mm, "end": v(0.73, -74.54) * mm});
            skArc(sketch, "E14.22.36.0", {"start": v(0, -76.2) * mm, "mid": v(0.35, -75.36) * mm, "end": v(0.73, -74.54) * mm});
            skLineSegment(sketch, "E14.26.36.0", {"start": v(0, -76.2) * mm, "end": v(0, -77.53) * mm});
            skArc(sketch, "E14.29.36.0", {"start": v(-0.8, -78.31) * mm, "mid": v(-0.23, -78.08) * mm, "end": v(0, -77.53) * mm});
            skArc(sketch, "E14.1.37.0", {"start": v(10.12, -76.86) * mm, "mid": v(10.42, -77.39) * mm, "end": v(11.01, -77.54) * mm});
            skLineSegment(sketch, "E14.4.37.0", {"start": v(9.95, -75.55) * mm, "end": v(10.12, -76.86) * mm});
            skArc(sketch, "E14.7.37.0", {"start": v(9.95, -75.55) * mm, "mid": v(9.5, -74.76) * mm, "end": v(9, -74) * mm});
            skArc(sketch, "E14.11.37.0", {"start": v(9, -74) * mm, "mid": v(8.66, -73.71) * mm, "end": v(8.23, -73.66) * mm});
            skLineSegment(sketch, "E14.15.37.0", {"start": v(8.23, -73.66) * mm, "end": v(7.9, -73.7) * mm});
            skArc(sketch, "E14.18.37.0", {"start": v(7.9, -73.7) * mm, "mid": v(7.5, -73.84) * mm, "end": v(7.23, -74.19) * mm});
            skArc(sketch, "E14.22.37.0", {"start": v(6.64, -75.91) * mm, "mid": v(6.91, -75.04) * mm, "end": v(7.23, -74.19) * mm});
            skLineSegment(sketch, "E14.26.37.0", {"start": v(6.64, -75.91) * mm, "end": v(6.76, -77.23) * mm});
            skArc(sketch, "E14.29.37.0", {"start": v(6.03, -78.08) * mm, "mid": v(6.57, -77.8) * mm, "end": v(6.76, -77.23) * mm});
            skArc(sketch, "E14.1.38.0", {"start": v(16.78, -75.69) * mm, "mid": v(17.13, -76.18) * mm, "end": v(17.73, -76.28) * mm});
            skLineSegment(sketch, "E14.4.38.0", {"start": v(16.5, -74.4) * mm, "end": v(16.78, -75.69) * mm});
            skArc(sketch, "E14.7.38.0", {"start": v(16.5, -74.4) * mm, "mid": v(15.97, -73.65) * mm, "end": v(15.42, -72.93) * mm});
            skArc(sketch, "E14.11.38.0", {"start": v(15.42, -72.93) * mm, "mid": v(15.06, -72.68) * mm, "end": v(14.62, -72.66) * mm});
            skLineSegment(sketch, "E14.15.38.0", {"start": v(14.62, -72.66) * mm, "end": v(14.3, -72.72) * mm});
            skArc(sketch, "E14.18.38.0", {"start": v(14.3, -72.72) * mm, "mid": v(13.9, -72.9) * mm, "end": v(13.66, -73.28) * mm});
            skArc(sketch, "E14.22.38.0", {"start": v(13.23, -75.04) * mm, "mid": v(13.43, -74.15) * mm, "end": v(13.66, -73.28) * mm});
            skLineSegment(sketch, "E14.26.38.0", {"start": v(13.23, -75.04) * mm, "end": v(13.46, -76.35) * mm});
            skArc(sketch, "E14.29.38.0", {"start": v(12.82, -77.26) * mm, "mid": v(13.33, -76.94) * mm, "end": v(13.46, -76.35) * mm});
            skArc(sketch, "E14.1.39.0", {"start": v(23.31, -73.94) * mm, "mid": v(23.7, -74.4) * mm, "end": v(24.3, -74.45) * mm});
            skLineSegment(sketch, "E14.4.39.0", {"start": v(22.91, -72.67) * mm, "end": v(23.31, -73.94) * mm});
            skArc(sketch, "E14.7.39.0", {"start": v(22.91, -72.67) * mm, "mid": v(22.33, -71.98) * mm, "end": v(21.71, -71.3) * mm});
            skArc(sketch, "E14.11.39.0", {"start": v(21.71, -71.3) * mm, "mid": v(21.33, -71.09) * mm, "end": v(20.9, -71.1) * mm});
            skLineSegment(sketch, "E14.15.39.0", {"start": v(20.9, -71.1) * mm, "end": v(20.58, -71.2) * mm});
            skArc(sketch, "E14.18.39.0", {"start": v(20.58, -71.2) * mm, "mid": v(20.2, -71.42) * mm, "end": v(20, -71.8) * mm});
            skArc(sketch, "E14.22.39.0", {"start": v(19.72, -73.6) * mm, "mid": v(19.84, -72.7) * mm, "end": v(20, -71.8) * mm});
            skLineSegment(sketch, "E14.26.39.0", {"start": v(19.72, -73.6) * mm, "end": v(20.07, -74.88) * mm});
            skArc(sketch, "E14.29.39.0", {"start": v(19.5, -75.85) * mm, "mid": v(19.98, -75.48) * mm, "end": v(20.07, -74.88) * mm});
            skArc(sketch, "E14.1.40.0", {"start": v(29.67, -71.62) * mm, "mid": v(30.1, -72.05) * mm, "end": v(30.7, -72.05) * mm});
            skLineSegment(sketch, "E14.4.40.0", {"start": v(29.16, -70.4) * mm, "end": v(29.67, -71.62) * mm});
            skArc(sketch, "E14.7.40.0", {"start": v(29.16, -70.4) * mm, "mid": v(28.52, -69.76) * mm, "end": v(27.85, -69.14) * mm});
            skArc(sketch, "E14.11.40.0", {"start": v(27.85, -69.14) * mm, "mid": v(27.45, -68.96) * mm, "end": v(27.01, -69.02) * mm});
            skLineSegment(sketch, "E14.15.40.0", {"start": v(27.01, -69.02) * mm, "end": v(26.71, -69.13) * mm});
            skArc(sketch, "E14.18.40.0", {"start": v(26.71, -69.13) * mm, "mid": v(26.35, -69.39) * mm, "end": v(26.18, -69.79) * mm});
            skArc(sketch, "E14.22.40.0", {"start": v(26.06, -71.6) * mm, "mid": v(26.1, -70.7) * mm, "end": v(26.18, -69.79) * mm});
            skLineSegment(sketch, "E14.26.40.0", {"start": v(26.06, -71.6) * mm, "end": v(26.52, -72.85) * mm});
            skArc(sketch, "E14.29.40.0", {"start": v(26.04, -73.86) * mm, "mid": v(26.49, -73.46) * mm, "end": v(26.52, -72.85) * mm});
            skArc(sketch, "E14.1.41.0", {"start": v(35.8, -68.77) * mm, "mid": v(36.26, -69.15) * mm, "end": v(36.87, -69.1) * mm});
            skLineSegment(sketch, "E14.4.41.0", {"start": v(35.19, -67.6) * mm, "end": v(35.8, -68.77) * mm});
            skArc(sketch, "E14.7.41.0", {"start": v(35.19, -67.6) * mm, "mid": v(34.49, -67) * mm, "end": v(33.77, -66.45) * mm});
            skArc(sketch, "E14.11.41.0", {"start": v(33.77, -66.45) * mm, "mid": v(33.35, -66.3) * mm, "end": v(32.93, -66.4) * mm});
            skLineSegment(sketch, "E14.15.41.0", {"start": v(32.93, -66.4) * mm, "end": v(32.63, -66.54) * mm});
            skArc(sketch, "E14.18.41.0", {"start": v(32.63, -66.54) * mm, "mid": v(32.3, -66.82) * mm, "end": v(32.16, -67.24) * mm});
            skArc(sketch, "E14.22.41.0", {"start": v(32.2, -69.06) * mm, "mid": v(32.16, -68.15) * mm, "end": v(32.16, -67.24) * mm});
            skLineSegment(sketch, "E14.26.41.0", {"start": v(32.2, -69.06) * mm, "end": v(32.76, -70.26) * mm});
            skArc(sketch, "E14.29.41.0", {"start": v(32.38, -71.31) * mm, "mid": v(32.79, -70.87) * mm, "end": v(32.76, -70.26) * mm});
            skArc(sketch, "E14.1.42.0", {"start": v(41.65, -65.38) * mm, "mid": v(42.15, -65.73) * mm, "end": v(42.75, -65.62) * mm});
            skLineSegment(sketch, "E14.4.42.0", {"start": v(40.94, -64.27) * mm, "end": v(41.65, -65.38) * mm});
            skArc(sketch, "E14.7.42.0", {"start": v(40.94, -64.27) * mm, "mid": v(40.2, -63.74) * mm, "end": v(39.43, -63.26) * mm});
            skArc(sketch, "E14.11.42.0", {"start": v(39.43, -63.26) * mm, "mid": v(39, -63.14) * mm, "end": v(38.59, -63.28) * mm});
            skLineSegment(sketch, "E14.15.42.0", {"start": v(38.59, -63.28) * mm, "end": v(38.3, -63.45) * mm});
            skArc(sketch, "E14.18.42.0", {"start": v(38.3, -63.45) * mm, "mid": v(38, -63.76) * mm, "end": v(37.9, -64.18) * mm});
            skArc(sketch, "E14.22.42.0", {"start": v(38.1, -66) * mm, "mid": v(37.98, -65.09) * mm, "end": v(37.9, -64.18) * mm});
            skLineSegment(sketch, "E14.26.42.0", {"start": v(38.1, -66) * mm, "end": v(38.76, -67.14) * mm});
            skArc(sketch, "E14.29.42.0", {"start": v(38.47, -68.22) * mm, "mid": v(38.84, -67.74) * mm, "end": v(38.76, -67.14) * mm});
            skArc(sketch, "E14.1.43.0", {"start": v(47.2, -61.5) * mm, "mid": v(47.72, -61.8) * mm, "end": v(48.3, -61.65) * mm});
            skLineSegment(sketch, "E14.4.43.0", {"start": v(46.39, -60.45) * mm, "end": v(47.2, -61.5) * mm});
            skArc(sketch, "E14.7.43.0", {"start": v(46.39, -60.45) * mm, "mid": v(45.6, -60) * mm, "end": v(44.8, -59.58) * mm});
            skArc(sketch, "E14.11.43.0", {"start": v(44.8, -59.58) * mm, "mid": v(44.36, -59.5) * mm, "end": v(43.96, -59.67) * mm});
            skLineSegment(sketch, "E14.15.43.0", {"start": v(43.96, -59.67) * mm, "end": v(43.7, -59.86) * mm});
            skArc(sketch, "E14.18.43.0", {"start": v(43.7, -59.86) * mm, "mid": v(43.41, -60.2) * mm, "end": v(43.35, -60.64) * mm});
            skArc(sketch, "E14.22.43.0", {"start": v(43.7, -62.42) * mm, "mid": v(43.5, -61.53) * mm, "end": v(43.35, -60.64) * mm});
            skLineSegment(sketch, "E14.26.43.0", {"start": v(43.7, -62.42) * mm, "end": v(44.47, -63.5) * mm});
            skArc(sketch, "E14.29.43.0", {"start": v(44.27, -64.6) * mm, "mid": v(44.6, -64.1) * mm, "end": v(44.47, -63.5) * mm});
            skArc(sketch, "E14.1.44.0", {"start": v(52.38, -57.16) * mm, "mid": v(52.93, -57.41) * mm, "end": v(53.5, -57.2) * mm});
            skLineSegment(sketch, "E14.4.44.0", {"start": v(51.48, -56.18) * mm, "end": v(52.38, -57.16) * mm});
            skArc(sketch, "E14.7.44.0", {"start": v(51.48, -56.18) * mm, "mid": v(50.66, -55.8) * mm, "end": v(49.82, -55.45) * mm});
            skArc(sketch, "E14.11.44.0", {"start": v(49.82, -55.45) * mm, "mid": v(49.38, -55.41) * mm, "end": v(48.99, -55.62) * mm});
            skLineSegment(sketch, "E14.15.44.0", {"start": v(48.99, -55.62) * mm, "end": v(48.75, -55.83) * mm});
            skArc(sketch, "E14.18.44.0", {"start": v(48.75, -55.83) * mm, "mid": v(48.5, -56.19) * mm, "end": v(48.47, -56.63) * mm});
            skArc(sketch, "E14.22.44.0", {"start": v(48.98, -58.37) * mm, "mid": v(48.7, -57.5) * mm, "end": v(48.47, -56.63) * mm});
            skLineSegment(sketch, "E14.26.44.0", {"start": v(48.98, -58.37) * mm, "end": v(49.83, -59.39) * mm});
            skArc(sketch, "E14.29.44.0", {"start": v(49.73, -60.5) * mm, "mid": v(50.01, -59.97) * mm, "end": v(49.83, -59.39) * mm});
            skArc(sketch, "E14.1.45.0", {"start": v(57.16, -52.38) * mm, "mid": v(57.73, -52.58) * mm, "end": v(58.28, -52.32) * mm});
            skLineSegment(sketch, "E14.4.45.0", {"start": v(56.18, -51.48) * mm, "end": v(57.16, -52.38) * mm});
            skArc(sketch, "E14.7.45.0", {"start": v(56.18, -51.48) * mm, "mid": v(55.33, -51.17) * mm, "end": v(54.46, -50.9) * mm});
            skArc(sketch, "E14.11.45.0", {"start": v(54.46, -50.9) * mm, "mid": v(54.02, -50.9) * mm, "end": v(53.65, -51.13) * mm});
            skLineSegment(sketch, "E14.15.45.0", {"start": v(53.65, -51.13) * mm, "end": v(53.43, -51.37) * mm});
            skArc(sketch, "E14.18.45.0", {"start": v(53.43, -51.37) * mm, "mid": v(53.2, -51.75) * mm, "end": v(53.22, -52.19) * mm});
            skArc(sketch, "E14.22.45.0", {"start": v(53.88, -53.88) * mm, "mid": v(53.53, -53.04) * mm, "end": v(53.22, -52.19) * mm});
            skLineSegment(sketch, "E14.26.45.0", {"start": v(53.88, -53.88) * mm, "end": v(54.82, -54.82) * mm});
            skArc(sketch, "E14.29.45.0", {"start": v(54.81, -55.94) * mm, "mid": v(55.05, -55.38) * mm, "end": v(54.82, -54.82) * mm});
            skArc(sketch, "E14.1.46.0", {"start": v(61.5, -47.2) * mm, "mid": v(62.1, -47.35) * mm, "end": v(62.61, -47.04) * mm});
            skLineSegment(sketch, "E14.4.46.0", {"start": v(60.45, -46.39) * mm, "end": v(61.5, -47.2) * mm});
            skArc(sketch, "E14.7.46.0", {"start": v(60.45, -46.39) * mm, "mid": v(59.58, -46.15) * mm, "end": v(58.69, -45.96) * mm});
            skArc(sketch, "E14.11.46.0", {"start": v(58.69, -45.96) * mm, "mid": v(58.25, -46) * mm, "end": v(57.9, -46.26) * mm});
            skLineSegment(sketch, "E14.15.46.0", {"start": v(57.9, -46.26) * mm, "end": v(57.7, -46.52) * mm});
            skArc(sketch, "E14.18.46.0", {"start": v(57.7, -46.52) * mm, "mid": v(57.51, -46.91) * mm, "end": v(57.57, -47.35) * mm});
            skArc(sketch, "E14.22.46.0", {"start": v(58.37, -48.98) * mm, "mid": v(57.95, -48.17) * mm, "end": v(57.57, -47.35) * mm});
            skLineSegment(sketch, "E14.26.46.0", {"start": v(58.37, -48.98) * mm, "end": v(59.39, -49.83) * mm});
            skArc(sketch, "E14.29.46.0", {"start": v(59.48, -50.95) * mm, "mid": v(59.67, -50.37) * mm, "end": v(59.39, -49.83) * mm});
            skArc(sketch, "E14.1.47.0", {"start": v(65.38, -41.65) * mm, "mid": v(65.98, -41.76) * mm, "end": v(66.48, -41.4) * mm});
            skLineSegment(sketch, "E14.4.47.0", {"start": v(64.27, -40.94) * mm, "end": v(65.38, -41.65) * mm});
            skArc(sketch, "E14.7.47.0", {"start": v(64.27, -40.94) * mm, "mid": v(63.37, -40.78) * mm, "end": v(62.47, -40.67) * mm});
            skArc(sketch, "E14.11.47.0", {"start": v(62.47, -40.67) * mm, "mid": v(62.04, -40.74) * mm, "end": v(61.71, -41.04) * mm});
            skLineSegment(sketch, "E14.15.47.0", {"start": v(61.71, -41.04) * mm, "end": v(61.53, -41.31) * mm});
            skArc(sketch, "E14.18.47.0", {"start": v(61.53, -41.31) * mm, "mid": v(61.38, -41.72) * mm, "end": v(61.48, -42.15) * mm});
            skArc(sketch, "E14.22.47.0", {"start": v(62.42, -43.7) * mm, "mid": v(61.93, -42.94) * mm, "end": v(61.48, -42.15) * mm});
            skLineSegment(sketch, "E14.26.47.0", {"start": v(62.42, -43.7) * mm, "end": v(63.5, -44.47) * mm});
            skArc(sketch, "E14.29.47.0", {"start": v(63.7, -45.57) * mm, "mid": v(63.83, -44.98) * mm, "end": v(63.5, -44.47) * mm});
            skArc(sketch, "E14.1.48.0", {"start": v(68.77, -35.8) * mm, "mid": v(69.37, -35.85) * mm, "end": v(69.83, -35.46) * mm});
            skLineSegment(sketch, "E14.4.48.0", {"start": v(67.6, -35.19) * mm, "end": v(68.77, -35.8) * mm});
            skArc(sketch, "E14.7.48.0", {"start": v(67.6, -35.19) * mm, "mid": v(66.68, -35.1) * mm, "end": v(65.78, -35.07) * mm});
            skArc(sketch, "E14.11.48.0", {"start": v(65.78, -35.07) * mm, "mid": v(65.35, -35.18) * mm, "end": v(65.06, -35.5) * mm});
            skLineSegment(sketch, "E14.15.48.0", {"start": v(65.06, -35.5) * mm, "end": v(64.9, -35.8) * mm});
            skArc(sketch, "E14.18.48.0", {"start": v(64.9, -35.8) * mm, "mid": v(64.79, -36.21) * mm, "end": v(64.92, -36.63) * mm});
            skArc(sketch, "E14.22.48.0", {"start": v(66, -38.1) * mm, "mid": v(65.44, -37.38) * mm, "end": v(64.92, -36.63) * mm});
            skLineSegment(sketch, "E14.26.48.0", {"start": v(66, -38.1) * mm, "end": v(67.14, -38.76) * mm});
            skArc(sketch, "E14.29.48.0", {"start": v(67.42, -39.85) * mm, "mid": v(67.5, -39.24) * mm, "end": v(67.14, -38.76) * mm});
            skArc(sketch, "E14.1.49.0", {"start": v(71.62, -29.67) * mm, "mid": v(72.23, -29.67) * mm, "end": v(72.66, -29.23) * mm});
            skLineSegment(sketch, "E14.4.49.0", {"start": v(70.4, -29.16) * mm, "end": v(71.62, -29.67) * mm});
            skArc(sketch, "E14.7.49.0", {"start": v(70.4, -29.16) * mm, "mid": v(69.5, -29.16) * mm, "end": v(68.58, -29.2) * mm});
            skArc(sketch, "E14.11.49.0", {"start": v(68.58, -29.2) * mm, "mid": v(68.17, -29.35) * mm, "end": v(67.9, -29.7) * mm});
            skLineSegment(sketch, "E14.15.49.0", {"start": v(67.9, -29.7) * mm, "end": v(67.77, -30) * mm});
            skArc(sketch, "E14.18.49.0", {"start": v(67.77, -30) * mm, "mid": v(67.7, -30.43) * mm, "end": v(67.86, -30.84) * mm});
            skArc(sketch, "E14.22.49.0", {"start": v(69.06, -32.2) * mm, "mid": v(68.45, -31.53) * mm, "end": v(67.86, -30.84) * mm});
            skLineSegment(sketch, "E14.26.49.0", {"start": v(69.06, -32.2) * mm, "end": v(70.26, -32.76) * mm});
            skArc(sketch, "E14.29.49.0", {"start": v(70.64, -33.82) * mm, "mid": v(70.67, -33.21) * mm, "end": v(70.26, -32.76) * mm});
            skArc(sketch, "E14.1.50.0", {"start": v(73.94, -23.31) * mm, "mid": v(74.54, -23.26) * mm, "end": v(74.93, -22.8) * mm});
            skLineSegment(sketch, "E14.4.50.0", {"start": v(72.67, -22.91) * mm, "end": v(73.94, -23.31) * mm});
            skArc(sketch, "E14.7.50.0", {"start": v(72.67, -22.91) * mm, "mid": v(71.77, -23) * mm, "end": v(70.87, -23.11) * mm});
            skArc(sketch, "E14.11.50.0", {"start": v(70.87, -23.11) * mm, "mid": v(70.47, -23.3) * mm, "end": v(70.23, -23.67) * mm});
            skLineSegment(sketch, "E14.15.50.0", {"start": v(70.23, -23.67) * mm, "end": v(70.13, -23.98) * mm});
            skArc(sketch, "E14.18.50.0", {"start": v(70.13, -23.98) * mm, "mid": v(70.1, -24.41) * mm, "end": v(70.3, -24.8) * mm});
            skArc(sketch, "E14.22.50.0", {"start": v(71.6, -26.06) * mm, "mid": v(70.93, -25.45) * mm, "end": v(70.3, -24.8) * mm});
            skLineSegment(sketch, "E14.26.50.0", {"start": v(71.6, -26.06) * mm, "end": v(72.85, -26.52) * mm});
            skArc(sketch, "E14.29.50.0", {"start": v(73.32, -27.53) * mm, "mid": v(73.3, -26.93) * mm, "end": v(72.85, -26.52) * mm});
            skArc(sketch, "E14.1.51.0", {"start": v(75.69, -16.78) * mm, "mid": v(76.28, -16.67) * mm, "end": v(76.63, -16.17) * mm});
            skLineSegment(sketch, "E14.4.51.0", {"start": v(74.4, -16.5) * mm, "end": v(75.69, -16.78) * mm});
            skArc(sketch, "E14.7.51.0", {"start": v(74.4, -16.5) * mm, "mid": v(73.5, -16.65) * mm, "end": v(72.61, -16.85) * mm});
            skArc(sketch, "E14.11.51.0", {"start": v(72.61, -16.85) * mm, "mid": v(72.23, -17.07) * mm, "end": v(72.03, -17.46) * mm});
            skLineSegment(sketch, "E14.15.51.0", {"start": v(72.03, -17.46) * mm, "end": v(71.95, -17.77) * mm});
            skArc(sketch, "E14.18.51.0", {"start": v(71.95, -17.77) * mm, "mid": v(71.95, -18.21) * mm, "end": v(72.19, -18.58) * mm});
            skArc(sketch, "E14.22.51.0", {"start": v(73.6, -19.72) * mm, "mid": v(72.88, -19.17) * mm, "end": v(72.19, -18.58) * mm});
            skLineSegment(sketch, "E14.26.51.0", {"start": v(73.6, -19.72) * mm, "end": v(74.88, -20.07) * mm});
            skArc(sketch, "E14.29.51.0", {"start": v(75.44, -21.04) * mm, "mid": v(75.36, -20.44) * mm, "end": v(74.88, -20.07) * mm});
            skArc(sketch, "E14.1.52.0", {"start": v(76.86, -10.12) * mm, "mid": v(77.45, -9.96) * mm, "end": v(77.75, -9.43) * mm});
            skLineSegment(sketch, "E14.4.52.0", {"start": v(75.55, -9.95) * mm, "end": v(76.86, -10.12) * mm});
            skArc(sketch, "E14.7.52.0", {"start": v(75.55, -9.95) * mm, "mid": v(74.67, -10.18) * mm, "end": v(73.8, -10.46) * mm});
            skArc(sketch, "E14.11.52.0", {"start": v(73.8, -10.46) * mm, "mid": v(73.44, -10.7) * mm, "end": v(73.28, -11.11) * mm});
            skLineSegment(sketch, "E14.15.52.0", {"start": v(73.28, -11.11) * mm, "end": v(73.23, -11.43) * mm});
            skArc(sketch, "E14.18.52.0", {"start": v(73.23, -11.43) * mm, "mid": v(73.26, -11.87) * mm, "end": v(73.53, -12.22) * mm});
            skArc(sketch, "E14.22.52.0", {"start": v(75.04, -13.23) * mm, "mid": v(74.27, -12.74) * mm, "end": v(73.53, -12.22) * mm});
            skLineSegment(sketch, "E14.26.52.0", {"start": v(75.04, -13.23) * mm, "end": v(76.35, -13.46) * mm});
            skArc(sketch, "E14.29.52.0", {"start": v(76.98, -14.38) * mm, "mid": v(76.86, -13.79) * mm, "end": v(76.35, -13.46) * mm});
            skArc(sketch, "E14.1.53.0", {"start": v(77.45, -3.38) * mm, "mid": v(78.02, -3.17) * mm, "end": v(78.27, -2.62) * mm});
            skLineSegment(sketch, "E14.4.53.0", {"start": v(76.13, -3.32) * mm, "end": v(77.45, -3.38) * mm});
            skArc(sketch, "E14.7.53.0", {"start": v(76.13, -3.32) * mm, "mid": v(75.27, -3.63) * mm, "end": v(74.43, -3.98) * mm});
            skArc(sketch, "E14.11.53.0", {"start": v(74.43, -3.98) * mm, "mid": v(74.1, -4.27) * mm, "end": v(73.97, -4.69) * mm});
            skLineSegment(sketch, "E14.15.53.0", {"start": v(73.97, -4.69) * mm, "end": v(73.94, -5) * mm});
            skArc(sketch, "E14.18.53.0", {"start": v(73.94, -5) * mm, "mid": v(74.02, -5.44) * mm, "end": v(74.32, -5.77) * mm});
            skArc(sketch, "E14.22.53.0", {"start": v(75.91, -6.64) * mm, "mid": v(75.1, -6.22) * mm, "end": v(74.32, -5.77) * mm});
            skLineSegment(sketch, "E14.26.53.0", {"start": v(75.91, -6.64) * mm, "end": v(77.23, -6.76) * mm});
            skArc(sketch, "E14.29.53.0", {"start": v(77.95, -7.62) * mm, "mid": v(77.77, -7.04) * mm, "end": v(77.23, -6.76) * mm});
            skArc(sketch, "E14.1.54.0", {"start": v(77.45, 3.38) * mm, "mid": v(78, 3.64) * mm, "end": v(78.2, 4.21) * mm});
            skLineSegment(sketch, "E14.4.54.0", {"start": v(76.13, 3.32) * mm, "end": v(77.45, 3.38) * mm});
            skArc(sketch, "E14.7.54.0", {"start": v(76.13, 3.32) * mm, "mid": v(75.3, 2.94) * mm, "end": v(74.5, 2.52) * mm});
            skArc(sketch, "E14.11.54.0", {"start": v(74.5, 2.52) * mm, "mid": v(74.19, 2.2) * mm, "end": v(74.1, 1.78) * mm});
            skLineSegment(sketch, "E14.15.54.0", {"start": v(74.1, 1.78) * mm, "end": v(74.1, 1.45) * mm});
            skArc(sketch, "E14.18.54.0", {"start": v(74.1, 1.45) * mm, "mid": v(74.21, 1.03) * mm, "end": v(74.54, 0.73) * mm});
            skArc(sketch, "E14.22.54.0", {"start": v(76.2, 0) * mm, "mid": v(75.36, 0.35) * mm, "end": v(74.54, 0.73) * mm});
            skLineSegment(sketch, "E14.26.54.0", {"start": v(76.2, 0) * mm, "end": v(77.53, 0) * mm});
            skArc(sketch, "E14.29.54.0", {"start": v(78.31, -0.8) * mm, "mid": v(78.08, -0.23) * mm, "end": v(77.53, 0) * mm});
            skArc(sketch, "E14.1.55.0", {"start": v(76.86, 10.12) * mm, "mid": v(77.39, 10.42) * mm, "end": v(77.54, 11.01) * mm});
            skLineSegment(sketch, "E14.4.55.0", {"start": v(75.55, 9.95) * mm, "end": v(76.86, 10.12) * mm});
            skArc(sketch, "E14.7.55.0", {"start": v(75.55, 9.95) * mm, "mid": v(74.76, 9.5) * mm, "end": v(74, 9) * mm});
            skArc(sketch, "E14.11.55.0", {"start": v(74, 9) * mm, "mid": v(73.71, 8.66) * mm, "end": v(73.66, 8.23) * mm});
            skLineSegment(sketch, "E14.15.55.0", {"start": v(73.66, 8.23) * mm, "end": v(73.7, 7.9) * mm});
            skArc(sketch, "E14.18.55.0", {"start": v(73.7, 7.9) * mm, "mid": v(73.84, 7.5) * mm, "end": v(74.19, 7.23) * mm});
            skArc(sketch, "E14.22.55.0", {"start": v(75.91, 6.64) * mm, "mid": v(75.04, 6.91) * mm, "end": v(74.19, 7.23) * mm});
            skLineSegment(sketch, "E14.26.55.0", {"start": v(75.91, 6.64) * mm, "end": v(77.23, 6.76) * mm});
            skArc(sketch, "E14.29.55.0", {"start": v(78.08, 6.03) * mm, "mid": v(77.8, 6.57) * mm, "end": v(77.23, 6.76) * mm});
            skArc(sketch, "E14.1.56.0", {"start": v(75.69, 16.78) * mm, "mid": v(76.18, 17.13) * mm, "end": v(76.28, 17.73) * mm});
            skLineSegment(sketch, "E14.4.56.0", {"start": v(74.4, 16.5) * mm, "end": v(75.69, 16.78) * mm});
            skArc(sketch, "E14.7.56.0", {"start": v(74.4, 16.5) * mm, "mid": v(73.65, 15.97) * mm, "end": v(72.93, 15.42) * mm});
            skArc(sketch, "E14.11.56.0", {"start": v(72.93, 15.42) * mm, "mid": v(72.68, 15.06) * mm, "end": v(72.66, 14.62) * mm});
            skLineSegment(sketch, "E14.15.56.0", {"start": v(72.66, 14.62) * mm, "end": v(72.72, 14.3) * mm});
            skArc(sketch, "E14.18.56.0", {"start": v(72.72, 14.3) * mm, "mid": v(72.9, 13.9) * mm, "end": v(73.28, 13.66) * mm});
            skArc(sketch, "E14.22.56.0", {"start": v(75.04, 13.23) * mm, "mid": v(74.15, 13.43) * mm, "end": v(73.28, 13.66) * mm});
            skLineSegment(sketch, "E14.26.56.0", {"start": v(75.04, 13.23) * mm, "end": v(76.35, 13.46) * mm});
            skArc(sketch, "E14.29.56.0", {"start": v(77.26, 12.82) * mm, "mid": v(76.94, 13.33) * mm, "end": v(76.35, 13.46) * mm});
            skArc(sketch, "E14.1.57.0", {"start": v(73.94, 23.31) * mm, "mid": v(74.4, 23.7) * mm, "end": v(74.45, 24.3) * mm});
            skLineSegment(sketch, "E14.4.57.0", {"start": v(72.67, 22.91) * mm, "end": v(73.94, 23.31) * mm});
            skArc(sketch, "E14.7.57.0", {"start": v(72.67, 22.91) * mm, "mid": v(71.98, 22.33) * mm, "end": v(71.3, 21.71) * mm});
            skArc(sketch, "E14.11.57.0", {"start": v(71.3, 21.71) * mm, "mid": v(71.09, 21.33) * mm, "end": v(71.1, 20.9) * mm});
            skLineSegment(sketch, "E14.15.57.0", {"start": v(71.1, 20.9) * mm, "end": v(71.2, 20.58) * mm});
            skArc(sketch, "E14.18.57.0", {"start": v(71.2, 20.58) * mm, "mid": v(71.42, 20.2) * mm, "end": v(71.8, 20) * mm});
            skArc(sketch, "E14.22.57.0", {"start": v(73.6, 19.72) * mm, "mid": v(72.7, 19.84) * mm, "end": v(71.8, 20) * mm});
            skLineSegment(sketch, "E14.26.57.0", {"start": v(73.6, 19.72) * mm, "end": v(74.88, 20.07) * mm});
            skArc(sketch, "E14.29.57.0", {"start": v(75.85, 19.5) * mm, "mid": v(75.48, 19.98) * mm, "end": v(74.88, 20.07) * mm});
            skArc(sketch, "E14.1.58.0", {"start": v(71.62, 29.67) * mm, "mid": v(72.05, 30.1) * mm, "end": v(72.05, 30.7) * mm});
            skLineSegment(sketch, "E14.4.58.0", {"start": v(70.4, 29.16) * mm, "end": v(71.62, 29.67) * mm});
            skArc(sketch, "E14.7.58.0", {"start": v(70.4, 29.16) * mm, "mid": v(69.76, 28.52) * mm, "end": v(69.14, 27.85) * mm});
            skArc(sketch, "E14.11.58.0", {"start": v(69.14, 27.85) * mm, "mid": v(68.96, 27.45) * mm, "end": v(69.02, 27.01) * mm});
            skLineSegment(sketch, "E14.15.58.0", {"start": v(69.02, 27.01) * mm, "end": v(69.13, 26.71) * mm});
            skArc(sketch, "E14.18.58.0", {"start": v(69.13, 26.71) * mm, "mid": v(69.39, 26.35) * mm, "end": v(69.79, 26.18) * mm});
            skArc(sketch, "E14.22.58.0", {"start": v(71.6, 26.06) * mm, "mid": v(70.7, 26.1) * mm, "end": v(69.79, 26.18) * mm});
            skLineSegment(sketch, "E14.26.58.0", {"start": v(71.6, 26.06) * mm, "end": v(72.85, 26.52) * mm});
            skArc(sketch, "E14.29.58.0", {"start": v(73.86, 26.04) * mm, "mid": v(73.46, 26.49) * mm, "end": v(72.85, 26.52) * mm});
            skArc(sketch, "E14.1.59.0", {"start": v(68.77, 35.8) * mm, "mid": v(69.15, 36.26) * mm, "end": v(69.1, 36.87) * mm});
            skLineSegment(sketch, "E14.4.59.0", {"start": v(67.6, 35.19) * mm, "end": v(68.77, 35.8) * mm});
            skArc(sketch, "E14.7.59.0", {"start": v(67.6, 35.19) * mm, "mid": v(67, 34.49) * mm, "end": v(66.45, 33.77) * mm});
            skArc(sketch, "E14.11.59.0", {"start": v(66.45, 33.77) * mm, "mid": v(66.3, 33.35) * mm, "end": v(66.4, 32.93) * mm});
            skLineSegment(sketch, "E14.15.59.0", {"start": v(66.4, 32.93) * mm, "end": v(66.54, 32.63) * mm});
            skArc(sketch, "E14.18.59.0", {"start": v(66.54, 32.63) * mm, "mid": v(66.82, 32.3) * mm, "end": v(67.24, 32.16) * mm});
            skArc(sketch, "E14.22.59.0", {"start": v(69.06, 32.2) * mm, "mid": v(68.15, 32.16) * mm, "end": v(67.24, 32.16) * mm});
            skLineSegment(sketch, "E14.26.59.0", {"start": v(69.06, 32.2) * mm, "end": v(70.26, 32.76) * mm});
            skArc(sketch, "E14.29.59.0", {"start": v(71.31, 32.38) * mm, "mid": v(70.87, 32.79) * mm, "end": v(70.26, 32.76) * mm});
            skArc(sketch, "E14.1.60.0", {"start": v(65.38, 41.65) * mm, "mid": v(65.73, 42.15) * mm, "end": v(65.62, 42.75) * mm});
            skLineSegment(sketch, "E14.4.60.0", {"start": v(64.27, 40.94) * mm, "end": v(65.38, 41.65) * mm});
            skArc(sketch, "E14.7.60.0", {"start": v(64.27, 40.94) * mm, "mid": v(63.74, 40.2) * mm, "end": v(63.26, 39.43) * mm});
            skArc(sketch, "E14.11.60.0", {"start": v(63.26, 39.43) * mm, "mid": v(63.14, 39) * mm, "end": v(63.28, 38.59) * mm});
            skLineSegment(sketch, "E14.15.60.0", {"start": v(63.28, 38.59) * mm, "end": v(63.45, 38.3) * mm});
            skArc(sketch, "E14.18.60.0", {"start": v(63.45, 38.3) * mm, "mid": v(63.76, 38) * mm, "end": v(64.18, 37.9) * mm});
            skArc(sketch, "E14.22.60.0", {"start": v(66, 38.1) * mm, "mid": v(65.09, 37.98) * mm, "end": v(64.18, 37.9) * mm});
            skLineSegment(sketch, "E14.26.60.0", {"start": v(66, 38.1) * mm, "end": v(67.14, 38.76) * mm});
            skArc(sketch, "E14.29.60.0", {"start": v(68.22, 38.47) * mm, "mid": v(67.74, 38.84) * mm, "end": v(67.14, 38.76) * mm});
            skArc(sketch, "E14.1.61.0", {"start": v(61.5, 47.2) * mm, "mid": v(61.8, 47.72) * mm, "end": v(61.65, 48.3) * mm});
            skLineSegment(sketch, "E14.4.61.0", {"start": v(60.45, 46.39) * mm, "end": v(61.5, 47.2) * mm});
            skArc(sketch, "E14.7.61.0", {"start": v(60.45, 46.39) * mm, "mid": v(60, 45.6) * mm, "end": v(59.58, 44.8) * mm});
            skArc(sketch, "E14.11.61.0", {"start": v(59.58, 44.8) * mm, "mid": v(59.5, 44.36) * mm, "end": v(59.67, 43.96) * mm});
            skLineSegment(sketch, "E14.15.61.0", {"start": v(59.67, 43.96) * mm, "end": v(59.86, 43.7) * mm});
            skArc(sketch, "E14.18.61.0", {"start": v(59.86, 43.7) * mm, "mid": v(60.2, 43.41) * mm, "end": v(60.64, 43.35) * mm});
            skArc(sketch, "E14.22.61.0", {"start": v(62.42, 43.7) * mm, "mid": v(61.53, 43.5) * mm, "end": v(60.64, 43.35) * mm});
            skLineSegment(sketch, "E14.26.61.0", {"start": v(62.42, 43.7) * mm, "end": v(63.5, 44.47) * mm});
            skArc(sketch, "E14.29.61.0", {"start": v(64.6, 44.27) * mm, "mid": v(64.1, 44.6) * mm, "end": v(63.5, 44.47) * mm});
            skArc(sketch, "E14.1.62.0", {"start": v(57.16, 52.38) * mm, "mid": v(57.41, 52.93) * mm, "end": v(57.2, 53.5) * mm});
            skLineSegment(sketch, "E14.4.62.0", {"start": v(56.18, 51.48) * mm, "end": v(57.16, 52.38) * mm});
            skArc(sketch, "E14.7.62.0", {"start": v(56.18, 51.48) * mm, "mid": v(55.8, 50.66) * mm, "end": v(55.45, 49.82) * mm});
            skArc(sketch, "E14.11.62.0", {"start": v(55.45, 49.82) * mm, "mid": v(55.41, 49.38) * mm, "end": v(55.62, 48.99) * mm});
            skLineSegment(sketch, "E14.15.62.0", {"start": v(55.62, 48.99) * mm, "end": v(55.83, 48.75) * mm});
            skArc(sketch, "E14.18.62.0", {"start": v(55.83, 48.75) * mm, "mid": v(56.19, 48.5) * mm, "end": v(56.63, 48.47) * mm});
            skArc(sketch, "E14.22.62.0", {"start": v(58.37, 48.98) * mm, "mid": v(57.5, 48.7) * mm, "end": v(56.63, 48.47) * mm});
            skLineSegment(sketch, "E14.26.62.0", {"start": v(58.37, 48.98) * mm, "end": v(59.39, 49.83) * mm});
            skArc(sketch, "E14.29.62.0", {"start": v(60.5, 49.73) * mm, "mid": v(59.97, 50.01) * mm, "end": v(59.39, 49.83) * mm});
            skArc(sketch, "E14.1.63.0", {"start": v(52.38, 57.16) * mm, "mid": v(52.58, 57.73) * mm, "end": v(52.32, 58.28) * mm});
            skLineSegment(sketch, "E14.4.63.0", {"start": v(51.48, 56.18) * mm, "end": v(52.38, 57.16) * mm});
            skArc(sketch, "E14.7.63.0", {"start": v(51.48, 56.18) * mm, "mid": v(51.17, 55.33) * mm, "end": v(50.9, 54.46) * mm});
            skArc(sketch, "E14.11.63.0", {"start": v(50.9, 54.46) * mm, "mid": v(50.9, 54.02) * mm, "end": v(51.13, 53.65) * mm});
            skLineSegment(sketch, "E14.15.63.0", {"start": v(51.13, 53.65) * mm, "end": v(51.37, 53.43) * mm});
            skArc(sketch, "E14.18.63.0", {"start": v(51.37, 53.43) * mm, "mid": v(51.75, 53.2) * mm, "end": v(52.19, 53.22) * mm});
            skArc(sketch, "E14.22.63.0", {"start": v(53.88, 53.88) * mm, "mid": v(53.04, 53.53) * mm, "end": v(52.19, 53.22) * mm});
            skLineSegment(sketch, "E14.26.63.0", {"start": v(53.88, 53.88) * mm, "end": v(54.82, 54.82) * mm});
            skArc(sketch, "E14.29.63.0", {"start": v(55.94, 54.81) * mm, "mid": v(55.38, 55.05) * mm, "end": v(54.82, 54.82) * mm});
            skArc(sketch, "E14.1.64.0", {"start": v(47.2, 61.5) * mm, "mid": v(47.35, 62.1) * mm, "end": v(47.04, 62.61) * mm});
            skLineSegment(sketch, "E14.4.64.0", {"start": v(46.39, 60.45) * mm, "end": v(47.2, 61.5) * mm});
            skArc(sketch, "E14.7.64.0", {"start": v(46.39, 60.45) * mm, "mid": v(46.15, 59.58) * mm, "end": v(45.96, 58.69) * mm});
            skArc(sketch, "E14.11.64.0", {"start": v(45.96, 58.69) * mm, "mid": v(46, 58.25) * mm, "end": v(46.26, 57.9) * mm});
            skLineSegment(sketch, "E14.15.64.0", {"start": v(46.26, 57.9) * mm, "end": v(46.52, 57.7) * mm});
            skArc(sketch, "E14.18.64.0", {"start": v(46.52, 57.7) * mm, "mid": v(46.91, 57.51) * mm, "end": v(47.35, 57.57) * mm});
            skArc(sketch, "E14.22.64.0", {"start": v(48.98, 58.37) * mm, "mid": v(48.17, 57.95) * mm, "end": v(47.35, 57.57) * mm});
            skLineSegment(sketch, "E14.26.64.0", {"start": v(48.98, 58.37) * mm, "end": v(49.83, 59.39) * mm});
            skArc(sketch, "E14.29.64.0", {"start": v(50.95, 59.48) * mm, "mid": v(50.37, 59.67) * mm, "end": v(49.83, 59.39) * mm});
            skArc(sketch, "E14.1.65.0", {"start": v(41.65, 65.38) * mm, "mid": v(41.76, 65.98) * mm, "end": v(41.4, 66.48) * mm});
            skLineSegment(sketch, "E14.4.65.0", {"start": v(40.94, 64.27) * mm, "end": v(41.65, 65.38) * mm});
            skArc(sketch, "E14.7.65.0", {"start": v(40.94, 64.27) * mm, "mid": v(40.78, 63.37) * mm, "end": v(40.67, 62.47) * mm});
            skArc(sketch, "E14.11.65.0", {"start": v(40.67, 62.47) * mm, "mid": v(40.74, 62.04) * mm, "end": v(41.04, 61.71) * mm});
            skLineSegment(sketch, "E14.15.65.0", {"start": v(41.04, 61.71) * mm, "end": v(41.31, 61.53) * mm});
            skArc(sketch, "E14.18.65.0", {"start": v(41.31, 61.53) * mm, "mid": v(41.72, 61.38) * mm, "end": v(42.15, 61.48) * mm});
            skArc(sketch, "E14.22.65.0", {"start": v(43.7, 62.42) * mm, "mid": v(42.94, 61.93) * mm, "end": v(42.15, 61.48) * mm});
            skLineSegment(sketch, "E14.26.65.0", {"start": v(43.7, 62.42) * mm, "end": v(44.47, 63.5) * mm});
            skArc(sketch, "E14.29.65.0", {"start": v(45.57, 63.7) * mm, "mid": v(44.98, 63.83) * mm, "end": v(44.47, 63.5) * mm});
            skArc(sketch, "E14.1.66.0", {"start": v(35.8, 68.77) * mm, "mid": v(35.85, 69.37) * mm, "end": v(35.46, 69.83) * mm});
            skLineSegment(sketch, "E14.4.66.0", {"start": v(35.19, 67.6) * mm, "end": v(35.8, 68.77) * mm});
            skArc(sketch, "E14.7.66.0", {"start": v(35.19, 67.6) * mm, "mid": v(35.1, 66.68) * mm, "end": v(35.07, 65.78) * mm});
            skArc(sketch, "E14.11.66.0", {"start": v(35.07, 65.78) * mm, "mid": v(35.18, 65.35) * mm, "end": v(35.5, 65.06) * mm});
            skLineSegment(sketch, "E14.15.66.0", {"start": v(35.5, 65.06) * mm, "end": v(35.8, 64.9) * mm});
            skArc(sketch, "E14.18.66.0", {"start": v(35.8, 64.9) * mm, "mid": v(36.21, 64.79) * mm, "end": v(36.63, 64.92) * mm});
            skArc(sketch, "E14.22.66.0", {"start": v(38.1, 66) * mm, "mid": v(37.38, 65.44) * mm, "end": v(36.63, 64.92) * mm});
            skLineSegment(sketch, "E14.26.66.0", {"start": v(38.1, 66) * mm, "end": v(38.76, 67.14) * mm});
            skArc(sketch, "E14.29.66.0", {"start": v(39.85, 67.42) * mm, "mid": v(39.24, 67.5) * mm, "end": v(38.76, 67.14) * mm});
            skArc(sketch, "E14.1.67.0", {"start": v(29.67, 71.62) * mm, "mid": v(29.67, 72.23) * mm, "end": v(29.23, 72.66) * mm});
            skLineSegment(sketch, "E14.4.67.0", {"start": v(29.16, 70.4) * mm, "end": v(29.67, 71.62) * mm});
            skArc(sketch, "E14.7.67.0", {"start": v(29.16, 70.4) * mm, "mid": v(29.16, 69.5) * mm, "end": v(29.2, 68.58) * mm});
            skArc(sketch, "E14.11.67.0", {"start": v(29.2, 68.58) * mm, "mid": v(29.35, 68.17) * mm, "end": v(29.7, 67.9) * mm});
            skLineSegment(sketch, "E14.15.67.0", {"start": v(29.7, 67.9) * mm, "end": v(30, 67.77) * mm});
            skArc(sketch, "E14.18.67.0", {"start": v(30, 67.77) * mm, "mid": v(30.43, 67.7) * mm, "end": v(30.84, 67.86) * mm});
            skArc(sketch, "E14.22.67.0", {"start": v(32.2, 69.06) * mm, "mid": v(31.53, 68.45) * mm, "end": v(30.84, 67.86) * mm});
            skLineSegment(sketch, "E14.26.67.0", {"start": v(32.2, 69.06) * mm, "end": v(32.76, 70.26) * mm});
            skArc(sketch, "E14.29.67.0", {"start": v(33.82, 70.64) * mm, "mid": v(33.21, 70.67) * mm, "end": v(32.76, 70.26) * mm});
            skArc(sketch, "E14.1.68.0", {"start": v(23.31, 73.94) * mm, "mid": v(23.26, 74.54) * mm, "end": v(22.8, 74.93) * mm});
            skLineSegment(sketch, "E14.4.68.0", {"start": v(22.91, 72.67) * mm, "end": v(23.31, 73.94) * mm});
            skArc(sketch, "E14.7.68.0", {"start": v(22.91, 72.67) * mm, "mid": v(23, 71.77) * mm, "end": v(23.11, 70.87) * mm});
            skArc(sketch, "E14.11.68.0", {"start": v(23.11, 70.87) * mm, "mid": v(23.3, 70.47) * mm, "end": v(23.67, 70.23) * mm});
            skLineSegment(sketch, "E14.15.68.0", {"start": v(23.67, 70.23) * mm, "end": v(23.98, 70.13) * mm});
            skArc(sketch, "E14.18.68.0", {"start": v(23.98, 70.13) * mm, "mid": v(24.41, 70.1) * mm, "end": v(24.8, 70.3) * mm});
            skArc(sketch, "E14.22.68.0", {"start": v(26.06, 71.6) * mm, "mid": v(25.45, 70.93) * mm, "end": v(24.8, 70.3) * mm});
            skLineSegment(sketch, "E14.26.68.0", {"start": v(26.06, 71.6) * mm, "end": v(26.52, 72.85) * mm});
            skArc(sketch, "E14.29.68.0", {"start": v(27.53, 73.32) * mm, "mid": v(26.93, 73.3) * mm, "end": v(26.52, 72.85) * mm});
            skArc(sketch, "E14.1.69.0", {"start": v(16.78, 75.69) * mm, "mid": v(16.67, 76.28) * mm, "end": v(16.17, 76.63) * mm});
            skLineSegment(sketch, "E14.4.69.0", {"start": v(16.5, 74.4) * mm, "end": v(16.78, 75.69) * mm});
            skArc(sketch, "E14.7.69.0", {"start": v(16.5, 74.4) * mm, "mid": v(16.65, 73.5) * mm, "end": v(16.85, 72.61) * mm});
            skArc(sketch, "E14.11.69.0", {"start": v(16.85, 72.61) * mm, "mid": v(17.07, 72.23) * mm, "end": v(17.46, 72.03) * mm});
            skLineSegment(sketch, "E14.15.69.0", {"start": v(17.46, 72.03) * mm, "end": v(17.77, 71.95) * mm});
            skArc(sketch, "E14.18.69.0", {"start": v(17.77, 71.95) * mm, "mid": v(18.21, 71.95) * mm, "end": v(18.58, 72.19) * mm});
            skArc(sketch, "E14.22.69.0", {"start": v(19.72, 73.6) * mm, "mid": v(19.17, 72.88) * mm, "end": v(18.58, 72.19) * mm});
            skLineSegment(sketch, "E14.26.69.0", {"start": v(19.72, 73.6) * mm, "end": v(20.07, 74.88) * mm});
            skArc(sketch, "E14.29.69.0", {"start": v(21.04, 75.44) * mm, "mid": v(20.44, 75.36) * mm, "end": v(20.07, 74.88) * mm});
            skArc(sketch, "E14.1.70.0", {"start": v(10.12, 76.86) * mm, "mid": v(9.96, 77.45) * mm, "end": v(9.43, 77.75) * mm});
            skLineSegment(sketch, "E14.4.70.0", {"start": v(9.95, 75.55) * mm, "end": v(10.12, 76.86) * mm});
            skArc(sketch, "E14.7.70.0", {"start": v(9.95, 75.55) * mm, "mid": v(10.18, 74.67) * mm, "end": v(10.46, 73.8) * mm});
            skArc(sketch, "E14.11.70.0", {"start": v(10.46, 73.8) * mm, "mid": v(10.7, 73.44) * mm, "end": v(11.11, 73.28) * mm});
            skLineSegment(sketch, "E14.15.70.0", {"start": v(11.11, 73.28) * mm, "end": v(11.43, 73.23) * mm});
            skArc(sketch, "E14.18.70.0", {"start": v(11.43, 73.23) * mm, "mid": v(11.87, 73.26) * mm, "end": v(12.22, 73.53) * mm});
            skArc(sketch, "E14.22.70.0", {"start": v(13.23, 75.04) * mm, "mid": v(12.74, 74.27) * mm, "end": v(12.22, 73.53) * mm});
            skLineSegment(sketch, "E14.26.70.0", {"start": v(13.23, 75.04) * mm, "end": v(13.46, 76.35) * mm});
            skArc(sketch, "E14.29.70.0", {"start": v(14.38, 76.98) * mm, "mid": v(13.79, 76.86) * mm, "end": v(13.46, 76.35) * mm});
            skArc(sketch, "E14.1.71.0", {"start": v(3.38, 77.45) * mm, "mid": v(3.17, 78.02) * mm, "end": v(2.62, 78.27) * mm});
            skLineSegment(sketch, "E14.4.71.0", {"start": v(3.32, 76.13) * mm, "end": v(3.38, 77.45) * mm});
            skArc(sketch, "E14.7.71.0", {"start": v(3.32, 76.13) * mm, "mid": v(3.63, 75.27) * mm, "end": v(3.98, 74.43) * mm});
            skArc(sketch, "E14.11.71.0", {"start": v(3.98, 74.43) * mm, "mid": v(4.27, 74.1) * mm, "end": v(4.69, 73.97) * mm});
            skLineSegment(sketch, "E14.15.71.0", {"start": v(4.69, 73.97) * mm, "end": v(5, 73.94) * mm});
            skArc(sketch, "E14.18.71.0", {"start": v(5, 73.94) * mm, "mid": v(5.44, 74.02) * mm, "end": v(5.77, 74.32) * mm});
            skArc(sketch, "E14.22.71.0", {"start": v(6.64, 75.91) * mm, "mid": v(6.22, 75.1) * mm, "end": v(5.77, 74.32) * mm});
            skLineSegment(sketch, "E14.26.71.0", {"start": v(6.64, 75.91) * mm, "end": v(6.76, 77.23) * mm});
            skArc(sketch, "E14.29.71.0", {"start": v(7.62, 77.95) * mm, "mid": v(7.04, 77.77) * mm, "end": v(6.76, 77.23) * mm});
            skArc(sketch, "E15.trimOffspring", {"start": v(2.62, 78.27) * mm, "mid": v(1.7, 78.3) * mm, "end": v(0.8, 78.31) * mm});
            skArc(sketch, "E16.trimOffspring", {"start": v(9.43, 77.75) * mm, "mid": v(8.53, 77.85) * mm, "end": v(7.62, 77.95) * mm});
            skArc(sketch, "E17.trimOffspring", {"start": v(-17.73, 76.28) * mm, "mid": v(-18.61, 76.07) * mm, "end": v(-19.5, 75.85) * mm});
            skArc(sketch, "E18.trimOffspring", {"start": v(-11.01, 77.54) * mm, "mid": v(-11.91, 77.4) * mm, "end": v(-12.82, 77.26) * mm});
            skArc(sketch, "E19.trimOffspring", {"start": v(16.17, 76.63) * mm, "mid": v(15.28, 76.81) * mm, "end": v(14.38, 76.98) * mm});
            skArc(sketch, "E20.trimOffspring", {"start": v(22.8, 74.93) * mm, "mid": v(21.92, 75.19) * mm, "end": v(21.04, 75.44) * mm});
            skArc(sketch, "E21.trimOffspring", {"start": v(29.23, 72.66) * mm, "mid": v(28.38, 73) * mm, "end": v(27.53, 73.32) * mm});
            skArc(sketch, "E22.trimOffspring", {"start": v(35.46, 69.83) * mm, "mid": v(34.64, 70.24) * mm, "end": v(33.82, 70.64) * mm});
            skArc(sketch, "E23.trimOffspring", {"start": v(41.4, 66.48) * mm, "mid": v(40.63, 66.95) * mm, "end": v(39.85, 67.42) * mm});
            skArc(sketch, "E24.trimOffspring", {"start": v(47.04, 62.61) * mm, "mid": v(46.3, 63.16) * mm, "end": v(45.57, 63.7) * mm});
            skArc(sketch, "E25.trimOffspring", {"start": v(-24.3, 74.45) * mm, "mid": v(-25.17, 74.16) * mm, "end": v(-26.04, 73.86) * mm});
            skArc(sketch, "E26.trimOffspring", {"start": v(-30.7, 72.05) * mm, "mid": v(-31.54, 71.68) * mm, "end": v(-32.38, 71.31) * mm});
            skArc(sketch, "E27.trimOffspring", {"start": v(-36.87, 69.1) * mm, "mid": v(-37.67, 68.66) * mm, "end": v(-38.47, 68.22) * mm});
            skArc(sketch, "E28.trimOffspring", {"start": v(-42.75, 65.62) * mm, "mid": v(-43.51, 65.12) * mm, "end": v(-44.27, 64.6) * mm});
            skArc(sketch, "E29.trimOffspring", {"start": v(-48.3, 61.65) * mm, "mid": v(-49.02, 61.08) * mm, "end": v(-49.73, 60.5) * mm});
            skArc(sketch, "E30.trimOffspring", {"start": v(-53.5, 57.2) * mm, "mid": v(-54.16, 56.57) * mm, "end": v(-54.81, 55.94) * mm});
            skArc(sketch, "E31.trimOffspring", {"start": v(52.32, 58.28) * mm, "mid": v(51.64, 58.88) * mm, "end": v(50.95, 59.48) * mm});
            skArc(sketch, "E32.trimOffspring", {"start": v(57.2, 53.5) * mm, "mid": v(56.57, 54.16) * mm, "end": v(55.94, 54.81) * mm});
            skArc(sketch, "E33.trimOffspring", {"start": v(61.65, 48.3) * mm, "mid": v(61.08, 49.02) * mm, "end": v(60.5, 49.73) * mm});
            skArc(sketch, "E34.trimOffspring", {"start": v(65.62, 42.75) * mm, "mid": v(65.12, 43.51) * mm, "end": v(64.6, 44.27) * mm});
            skArc(sketch, "E35.trimOffspring", {"start": v(69.1, 36.87) * mm, "mid": v(68.66, 37.67) * mm, "end": v(68.22, 38.47) * mm});
            skArc(sketch, "E36.trimOffspring", {"start": v(-58.28, 52.32) * mm, "mid": v(-58.88, 51.64) * mm, "end": v(-59.48, 50.95) * mm});
            skArc(sketch, "E37.trimOffspring", {"start": v(-62.61, 47.04) * mm, "mid": v(-63.16, 46.3) * mm, "end": v(-63.7, 45.57) * mm});
            skArc(sketch, "E38.trimOffspring", {"start": v(-66.48, 41.4) * mm, "mid": v(-66.95, 40.63) * mm, "end": v(-67.42, 39.85) * mm});
            skArc(sketch, "E39.trimOffspring", {"start": v(72.05, 30.7) * mm, "mid": v(71.68, 31.54) * mm, "end": v(71.31, 32.38) * mm});
            skArc(sketch, "E40.trimOffspring", {"start": v(74.45, 24.3) * mm, "mid": v(74.16, 25.17) * mm, "end": v(73.86, 26.04) * mm});
            skArc(sketch, "E41.trimOffspring", {"start": v(76.28, 17.73) * mm, "mid": v(76.07, 18.61) * mm, "end": v(75.85, 19.5) * mm});
            skArc(sketch, "E42.trimOffspring", {"start": v(-69.83, 35.46) * mm, "mid": v(-70.24, 34.64) * mm, "end": v(-70.64, 33.82) * mm});
            skArc(sketch, "E43.trimOffspring", {"start": v(77.54, 11.01) * mm, "mid": v(77.4, 11.91) * mm, "end": v(77.26, 12.82) * mm});
            skArc(sketch, "E44.trimOffspring", {"start": v(78.2, 4.21) * mm, "mid": v(78.15, 5.12) * mm, "end": v(78.08, 6.03) * mm});
            skArc(sketch, "E45.trimOffspring", {"start": v(78.27, -2.62) * mm, "mid": v(78.3, -1.7) * mm, "end": v(78.31, -0.8) * mm});
            skArc(sketch, "E46.trimOffspring", {"start": v(77.75, -9.43) * mm, "mid": v(77.85, -8.53) * mm, "end": v(77.95, -7.62) * mm});
            skArc(sketch, "E47.trimOffspring", {"start": v(76.63, -16.17) * mm, "mid": v(76.81, -15.28) * mm, "end": v(76.98, -14.38) * mm});
            skArc(sketch, "E48.trimOffspring", {"start": v(74.93, -22.8) * mm, "mid": v(75.19, -21.92) * mm, "end": v(75.44, -21.04) * mm});
            skArc(sketch, "E49.trimOffspring", {"start": v(72.66, -29.23) * mm, "mid": v(73, -28.38) * mm, "end": v(73.32, -27.53) * mm});
            skArc(sketch, "E50.trimOffspring", {"start": v(69.83, -35.46) * mm, "mid": v(70.24, -34.64) * mm, "end": v(70.64, -33.82) * mm});
            skArc(sketch, "E51.trimOffspring", {"start": v(66.48, -41.4) * mm, "mid": v(66.95, -40.63) * mm, "end": v(67.42, -39.85) * mm});
            skArc(sketch, "E52.trimOffspring", {"start": v(62.61, -47.04) * mm, "mid": v(63.16, -46.3) * mm, "end": v(63.7, -45.57) * mm});
            skArc(sketch, "E53.trimOffspring", {"start": v(58.28, -52.32) * mm, "mid": v(58.88, -51.64) * mm, "end": v(59.48, -50.95) * mm});
            skArc(sketch, "E54.trimOffspring", {"start": v(53.5, -57.2) * mm, "mid": v(54.16, -56.57) * mm, "end": v(54.81, -55.94) * mm});
            skArc(sketch, "E55.trimOffspring", {"start": v(48.3, -61.65) * mm, "mid": v(49.02, -61.08) * mm, "end": v(49.73, -60.5) * mm});
            skArc(sketch, "E56.trimOffspring", {"start": v(42.75, -65.62) * mm, "mid": v(43.51, -65.12) * mm, "end": v(44.27, -64.6) * mm});
            skArc(sketch, "E57.trimOffspring", {"start": v(36.87, -69.1) * mm, "mid": v(37.67, -68.66) * mm, "end": v(38.47, -68.22) * mm});
            skArc(sketch, "E58.trimOffspring", {"start": v(30.7, -72.05) * mm, "mid": v(31.54, -71.68) * mm, "end": v(32.38, -71.31) * mm});
            skArc(sketch, "E59.trimOffspring", {"start": v(24.3, -74.45) * mm, "mid": v(25.17, -74.16) * mm, "end": v(26.04, -73.86) * mm});
            skArc(sketch, "E60.trimOffspring", {"start": v(17.73, -76.28) * mm, "mid": v(18.61, -76.07) * mm, "end": v(19.5, -75.85) * mm});
            skArc(sketch, "E61.trimOffspring", {"start": v(11.01, -77.54) * mm, "mid": v(11.91, -77.4) * mm, "end": v(12.82, -77.26) * mm});
            skArc(sketch, "E62.trimOffspring", {"start": v(4.21, -78.2) * mm, "mid": v(5.12, -78.15) * mm, "end": v(6.03, -78.08) * mm});
            skArc(sketch, "E63.trimOffspring", {"start": v(-2.62, -78.27) * mm, "mid": v(-1.7, -78.3) * mm, "end": v(-0.8, -78.31) * mm});
            skArc(sketch, "E64.trimOffspring", {"start": v(-9.43, -77.75) * mm, "mid": v(-8.53, -77.85) * mm, "end": v(-7.62, -77.95) * mm});
            skArc(sketch, "E65.trimOffspring", {"start": v(-16.17, -76.63) * mm, "mid": v(-15.28, -76.81) * mm, "end": v(-14.38, -76.98) * mm});
            skArc(sketch, "E66.trimOffspring", {"start": v(-22.8, -74.93) * mm, "mid": v(-21.92, -75.19) * mm, "end": v(-21.04, -75.44) * mm});
            skArc(sketch, "E67.trimOffspring", {"start": v(-29.23, -72.66) * mm, "mid": v(-28.38, -73) * mm, "end": v(-27.53, -73.32) * mm});
            skArc(sketch, "E68.trimOffspring", {"start": v(-35.46, -69.83) * mm, "mid": v(-34.64, -70.24) * mm, "end": v(-33.82, -70.64) * mm});
            skArc(sketch, "E69.trimOffspring", {"start": v(-41.4, -66.48) * mm, "mid": v(-40.63, -66.95) * mm, "end": v(-39.85, -67.42) * mm});
            skArc(sketch, "E70.trimOffspring", {"start": v(-47.04, -62.61) * mm, "mid": v(-46.3, -63.16) * mm, "end": v(-45.57, -63.7) * mm});
            skArc(sketch, "E71.trimOffspring", {"start": v(-52.32, -58.28) * mm, "mid": v(-51.64, -58.88) * mm, "end": v(-50.95, -59.48) * mm});
            skArc(sketch, "E72.trimOffspring", {"start": v(-57.2, -53.5) * mm, "mid": v(-56.57, -54.16) * mm, "end": v(-55.94, -54.81) * mm});
            skArc(sketch, "E73.trimOffspring", {"start": v(-61.65, -48.3) * mm, "mid": v(-61.08, -49.02) * mm, "end": v(-60.5, -49.73) * mm});
            skArc(sketch, "E74.trimOffspring", {"start": v(-65.62, -42.75) * mm, "mid": v(-65.12, -43.51) * mm, "end": v(-64.6, -44.27) * mm});
            skArc(sketch, "E75.trimOffspring", {"start": v(-69.1, -36.87) * mm, "mid": v(-68.66, -37.67) * mm, "end": v(-68.22, -38.47) * mm});
            skArc(sketch, "E76.trimOffspring", {"start": v(-72.05, -30.7) * mm, "mid": v(-71.68, -31.54) * mm, "end": v(-71.31, -32.38) * mm});
            skArc(sketch, "E77.trimOffspring", {"start": v(-74.45, -24.3) * mm, "mid": v(-74.16, -25.17) * mm, "end": v(-73.86, -26.04) * mm});
            skArc(sketch, "E78.trimOffspring", {"start": v(-76.28, -17.73) * mm, "mid": v(-76.07, -18.61) * mm, "end": v(-75.85, -19.5) * mm});
            skArc(sketch, "E79.trimOffspring", {"start": v(-77.54, -11.01) * mm, "mid": v(-77.4, -11.91) * mm, "end": v(-77.26, -12.82) * mm});
            skArc(sketch, "E80.trimOffspring", {"start": v(-78.2, -4.21) * mm, "mid": v(-78.15, -5.12) * mm, "end": v(-78.08, -6.03) * mm});
            skArc(sketch, "E81.trimOffspring", {"start": v(-78.27, 2.62) * mm, "mid": v(-78.3, 1.7) * mm, "end": v(-78.31, 0.8) * mm});
            skArc(sketch, "E82.trimOffspring", {"start": v(-77.75, 9.43) * mm, "mid": v(-77.85, 8.53) * mm, "end": v(-77.95, 7.62) * mm});
            skArc(sketch, "E83.trimOffspring", {"start": v(-76.63, 16.17) * mm, "mid": v(-76.81, 15.28) * mm, "end": v(-76.98, 14.38) * mm});
            skArc(sketch, "E84.trimOffspring", {"start": v(-74.93, 22.8) * mm, "mid": v(-75.19, 21.92) * mm, "end": v(-75.44, 21.04) * mm});
            skArc(sketch, "E85.trimOffspring", {"start": v(-72.66, 29.23) * mm, "mid": v(-73, 28.38) * mm, "end": v(-73.32, 27.53) * mm});
            skSolve(sketch);
        }
        {
            var Q0;
            Q0=makeQuery(id+"F0.imprint","IMPRINT",FACE,{"disambiguationData":[TD([[makeQuery(id+"F0.imprint","IMPRINT",EDGE,{"derivedFrom":sQuery(id+"F0.wireOp",EDGE,"E0")}),1.0]])]});
            extrude(context, id + "F1", {"entities" : qUnion([Q0]), "depth" : 6.35 * mm});
        }
        {
            var Q0;
            Q0=makeQuery(id+"F0.imprint","IMPRINT",FACE,{"disambiguationData":[TD([[makeQuery(id+"F0.imprint","IMPRINT",EDGE,{"derivedFrom":sQuery(id+"F0.wireOp",EDGE,"E0")}),-1.0]])]});
            extrude(context, id + "F2", {"entities" : qUnion([Q0]), "operationType" : NewBodyOperationType.ADD, "depth" : 19.05 * mm});
        }
        {
            var Q0;
            Q0=makeQuery(id+"F1.opExtrude","CAP_FACE",FACE,{"disambiguationData":[OSD([sQuery(id+"F0.wireOp",EDGE,"E0"),sQuery(id+"F0.wireOp",EDGE,"E1.MirrorCS"),sQuery(id+"F0.wireOp",EDGE,"E2.MirrorCS"),sQuery(id+"F0.wireOp",EDGE,"E3.MirrorCS"),sQuery(id+"F0.wireOp",EDGE,"E4.MirrorCS"),sQuery(id+"F0.wireOp",EDGE,"E5.filletArc"),sQuery(id+"F0.wireOp",EDGE,"E6.filletArc"),sQuery(id+"F0.wireOp",EDGE,"E7"),sQuery(id+"F0.wireOp",EDGE,"E11.filletArc"),sQuery(id+"F0.wireOp",EDGE,"E12.filletArc"),sQuery(id+"F0.wireOp",EDGE,"E13.1.0"),sQuery(id+"F0.wireOp",EDGE,"E13.1.1"),sQuery(id+"F0.wireOp",EDGE,"E13.1.2"),sQuery(id+"F0.wireOp",EDGE,"E13.1.3"),sQuery(id+"F0.wireOp",EDGE,"E13.1.4"),sQuery(id+"F0.wireOp",EDGE,"E13.1.5"),sQuery(id+"F0.wireOp",EDGE,"E13.1.6"),sQuery(id+"F0.wireOp",EDGE,"E13.1.7"),sQuery(id+"F0.wireOp",EDGE,"E13.1.8"),sQuery(id+"F0.wireOp",EDGE,"E13.2.0"),sQuery(id+"F0.wireOp",EDGE,"E13.2.1"),sQuery(id+"F0.wireOp",EDGE,"E13.2.2"),sQuery(id+"F0.wireOp",EDGE,"E13.2.3"),sQuery(id+"F0.wireOp",EDGE,"E13.2.4"),sQuery(id+"F0.wireOp",EDGE,"E13.2.5"),sQuery(id+"F0.wireOp",EDGE,"E13.2.6"),sQuery(id+"F0.wireOp",EDGE,"E13.2.7"),sQuery(id+"F0.wireOp",EDGE,"E13.2.8"),sQuery(id+"F0.wireOp",EDGE,"E14.1.3.0"),sQuery(id+"F0.wireOp",EDGE,"E14.4.3.0"),sQuery(id+"F0.wireOp",EDGE,"E14.7.3.0"),sQuery(id+"F0.wireOp",EDGE,"E14.11.3.0"),sQuery(id+"F0.wireOp",EDGE,"E14.15.3.0"),sQuery(id+"F0.wireOp",EDGE,"E14.18.3.0"),sQuery(id+"F0.wireOp",EDGE,"E14.22.3.0"),sQuery(id+"F0.wireOp",EDGE,"E14.26.3.0"),sQuery(id+"F0.wireOp",EDGE,"E14.29.3.0"),sQuery(id+"F0.wireOp",EDGE,"E14.1.4.0"),sQuery(id+"F0.wireOp",EDGE,"E14.4.4.0"),sQuery(id+"F0.wireOp",EDGE,"E14.7.4.0"),sQuery(id+"F0.wireOp",EDGE,"E14.11.4.0"),sQuery(id+"F0.wireOp",EDGE,"E14.15.4.0"),sQuery(id+"F0.wireOp",EDGE,"E14.18.4.0"),sQuery(id+"F0.wireOp",EDGE,"E14.22.4.0"),sQuery(id+"F0.wireOp",EDGE,"E14.26.4.0"),sQuery(id+"F0.wireOp",EDGE,"E14.29.4.0"),sQuery(id+"F0.wireOp",EDGE,"E14.1.5.0"),sQuery(id+"F0.wireOp",EDGE,"E14.4.5.0"),sQuery(id+"F0.wireOp",EDGE,"E14.7.5.0"),sQuery(id+"F0.wireOp",EDGE,"E14.11.5.0"),sQuery(id+"F0.wireOp",EDGE,"E14.15.5.0"),sQuery(id+"F0.wireOp",EDGE,"E14.18.5.0"),sQuery(id+"F0.wireOp",EDGE,"E14.22.5.0"),sQuery(id+"F0.wireOp",EDGE,"E14.26.5.0"),sQuery(id+"F0.wireOp",EDGE,"E14.29.5.0"),sQuery(id+"F0.wireOp",EDGE,"E14.1.6.0"),sQuery(id+"F0.wireOp",EDGE,"E14.4.6.0"),sQuery(id+"F0.wireOp",EDGE,"E14.7.6.0"),sQuery(id+"F0.wireOp",EDGE,"E14.11.6.0"),sQuery(id+"F0.wireOp",EDGE,"E14.15.6.0"),sQuery(id+"F0.wireOp",EDGE,"E14.18.6.0"),sQuery(id+"F0.wireOp",EDGE,"E14.22.6.0"),sQuery(id+"F0.wireOp",EDGE,"E14.26.6.0"),sQuery(id+"F0.wireOp",EDGE,"E14.29.6.0"),sQuery(id+"F0.wireOp",EDGE,"E14.1.7.0"),sQuery(id+"F0.wireOp",EDGE,"E14.4.7.0"),sQuery(id+"F0.wireOp",EDGE,"E14.7.7.0"),sQuery(id+"F0.wireOp",EDGE,"E14.11.7.0"),sQuery(id+"F0.wireOp",EDGE,"E14.15.7.0"),sQuery(id+"F0.wireOp",EDGE,"E14.18.7.0"),sQuery(id+"F0.wireOp",EDGE,"E14.22.7.0"),sQuery(id+"F0.wireOp",EDGE,"E14.26.7.0"),sQuery(id+"F0.wireOp",EDGE,"E14.29.7.0"),sQuery(id+"F0.wireOp",EDGE,"E14.1.8.0"),sQuery(id+"F0.wireOp",EDGE,"E14.4.8.0"),sQuery(id+"F0.wireOp",EDGE,"E14.7.8.0"),sQuery(id+"F0.wireOp",EDGE,"E14.11.8.0"),sQuery(id+"F0.wireOp",EDGE,"E14.15.8.0"),sQuery(id+"F0.wireOp",EDGE,"E14.18.8.0"),sQuery(id+"F0.wireOp",EDGE,"E14.22.8.0"),sQuery(id+"F0.wireOp",EDGE,"E14.26.8.0"),sQuery(id+"F0.wireOp",EDGE,"E14.29.8.0"),sQuery(id+"F0.wireOp",EDGE,"E14.1.9.0"),sQuery(id+"F0.wireOp",EDGE,"E14.4.9.0"),sQuery(id+"F0.wireOp",EDGE,"E14.7.9.0"),sQuery(id+"F0.wireOp",EDGE,"E14.11.9.0"),sQuery(id+"F0.wireOp",EDGE,"E14.15.9.0"),sQuery(id+"F0.wireOp",EDGE,"E14.18.9.0"),sQuery(id+"F0.wireOp",EDGE,"E14.22.9.0"),sQuery(id+"F0.wireOp",EDGE,"E14.26.9.0"),sQuery(id+"F0.wireOp",EDGE,"E14.29.9.0"),sQuery(id+"F0.wireOp",EDGE,"E14.1.10.0"),sQuery(id+"F0.wireOp",EDGE,"E14.4.10.0"),sQuery(id+"F0.wireOp",EDGE,"E14.7.10.0"),sQuery(id+"F0.wireOp",EDGE,"E14.11.10.0"),sQuery(id+"F0.wireOp",EDGE,"E14.15.10.0"),sQuery(id+"F0.wireOp",EDGE,"E14.18.10.0"),sQuery(id+"F0.wireOp",EDGE,"E14.22.10.0"),sQuery(id+"F0.wireOp",EDGE,"E14.26.10.0"),sQuery(id+"F0.wireOp",EDGE,"E14.29.10.0"),sQuery(id+"F0.wireOp",EDGE,"E14.1.11.0"),sQuery(id+"F0.wireOp",EDGE,"E14.4.11.0"),sQuery(id+"F0.wireOp",EDGE,"E14.7.11.0"),sQuery(id+"F0.wireOp",EDGE,"E14.11.11.0"),sQuery(id+"F0.wireOp",EDGE,"E14.15.11.0"),sQuery(id+"F0.wireOp",EDGE,"E14.18.11.0"),sQuery(id+"F0.wireOp",EDGE,"E14.22.11.0"),sQuery(id+"F0.wireOp",EDGE,"E14.26.11.0"),sQuery(id+"F0.wireOp",EDGE,"E14.29.11.0"),sQuery(id+"F0.wireOp",EDGE,"E14.1.12.0"),sQuery(id+"F0.wireOp",EDGE,"E14.4.12.0"),sQuery(id+"F0.wireOp",EDGE,"E14.7.12.0"),sQuery(id+"F0.wireOp",EDGE,"E14.11.12.0"),sQuery(id+"F0.wireOp",EDGE,"E14.15.12.0"),sQuery(id+"F0.wireOp",EDGE,"E14.18.12.0"),sQuery(id+"F0.wireOp",EDGE,"E14.22.12.0"),sQuery(id+"F0.wireOp",EDGE,"E14.26.12.0"),sQuery(id+"F0.wireOp",EDGE,"E14.29.12.0"),sQuery(id+"F0.wireOp",EDGE,"E14.1.13.0"),sQuery(id+"F0.wireOp",EDGE,"E14.4.13.0"),sQuery(id+"F0.wireOp",EDGE,"E14.7.13.0"),sQuery(id+"F0.wireOp",EDGE,"E14.11.13.0"),sQuery(id+"F0.wireOp",EDGE,"E14.15.13.0"),sQuery(id+"F0.wireOp",EDGE,"E14.18.13.0"),sQuery(id+"F0.wireOp",EDGE,"E14.22.13.0"),sQuery(id+"F0.wireOp",EDGE,"E14.26.13.0"),sQuery(id+"F0.wireOp",EDGE,"E14.29.13.0"),sQuery(id+"F0.wireOp",EDGE,"E14.1.14.0"),sQuery(id+"F0.wireOp",EDGE,"E14.4.14.0"),sQuery(id+"F0.wireOp",EDGE,"E14.7.14.0"),sQuery(id+"F0.wireOp",EDGE,"E14.11.14.0"),sQuery(id+"F0.wireOp",EDGE,"E14.15.14.0"),sQuery(id+"F0.wireOp",EDGE,"E14.18.14.0"),sQuery(id+"F0.wireOp",EDGE,"E14.22.14.0"),sQuery(id+"F0.wireOp",EDGE,"E14.26.14.0"),sQuery(id+"F0.wireOp",EDGE,"E14.29.14.0"),sQuery(id+"F0.wireOp",EDGE,"E14.1.15.0"),sQuery(id+"F0.wireOp",EDGE,"E14.4.15.0"),sQuery(id+"F0.wireOp",EDGE,"E14.7.15.0"),sQuery(id+"F0.wireOp",EDGE,"E14.11.15.0"),sQuery(id+"F0.wireOp",EDGE,"E14.15.15.0"),sQuery(id+"F0.wireOp",EDGE,"E14.18.15.0"),sQuery(id+"F0.wireOp",EDGE,"E14.22.15.0"),sQuery(id+"F0.wireOp",EDGE,"E14.26.15.0"),sQuery(id+"F0.wireOp",EDGE,"E14.29.15.0"),sQuery(id+"F0.wireOp",EDGE,"E14.1.16.0"),sQuery(id+"F0.wireOp",EDGE,"E14.4.16.0"),sQuery(id+"F0.wireOp",EDGE,"E14.7.16.0"),sQuery(id+"F0.wireOp",EDGE,"E14.11.16.0"),sQuery(id+"F0.wireOp",EDGE,"E14.15.16.0"),sQuery(id+"F0.wireOp",EDGE,"E14.18.16.0"),sQuery(id+"F0.wireOp",EDGE,"E14.22.16.0"),sQuery(id+"F0.wireOp",EDGE,"E14.26.16.0"),sQuery(id+"F0.wireOp",EDGE,"E14.29.16.0"),sQuery(id+"F0.wireOp",EDGE,"E14.1.17.0"),sQuery(id+"F0.wireOp",EDGE,"E14.4.17.0"),sQuery(id+"F0.wireOp",EDGE,"E14.7.17.0"),sQuery(id+"F0.wireOp",EDGE,"E14.11.17.0"),sQuery(id+"F0.wireOp",EDGE,"E14.15.17.0"),sQuery(id+"F0.wireOp",EDGE,"E14.18.17.0"),sQuery(id+"F0.wireOp",EDGE,"E14.22.17.0"),sQuery(id+"F0.wireOp",EDGE,"E14.26.17.0"),sQuery(id+"F0.wireOp",EDGE,"E14.29.17.0"),sQuery(id+"F0.wireOp",EDGE,"E14.1.18.0"),sQuery(id+"F0.wireOp",EDGE,"E14.4.18.0"),sQuery(id+"F0.wireOp",EDGE,"E14.7.18.0"),sQuery(id+"F0.wireOp",EDGE,"E14.11.18.0"),sQuery(id+"F0.wireOp",EDGE,"E14.15.18.0"),sQuery(id+"F0.wireOp",EDGE,"E14.18.18.0"),sQuery(id+"F0.wireOp",EDGE,"E14.22.18.0"),sQuery(id+"F0.wireOp",EDGE,"E14.26.18.0"),sQuery(id+"F0.wireOp",EDGE,"E14.29.18.0"),sQuery(id+"F0.wireOp",EDGE,"E14.1.19.0"),sQuery(id+"F0.wireOp",EDGE,"E14.4.19.0"),sQuery(id+"F0.wireOp",EDGE,"E14.7.19.0"),sQuery(id+"F0.wireOp",EDGE,"E14.11.19.0"),sQuery(id+"F0.wireOp",EDGE,"E14.15.19.0"),sQuery(id+"F0.wireOp",EDGE,"E14.18.19.0"),sQuery(id+"F0.wireOp",EDGE,"E14.22.19.0"),sQuery(id+"F0.wireOp",EDGE,"E14.26.19.0"),sQuery(id+"F0.wireOp",EDGE,"E14.29.19.0"),sQuery(id+"F0.wireOp",EDGE,"E14.1.20.0"),sQuery(id+"F0.wireOp",EDGE,"E14.4.20.0"),sQuery(id+"F0.wireOp",EDGE,"E14.7.20.0"),sQuery(id+"F0.wireOp",EDGE,"E14.11.20.0"),sQuery(id+"F0.wireOp",EDGE,"E14.15.20.0"),sQuery(id+"F0.wireOp",EDGE,"E14.18.20.0"),sQuery(id+"F0.wireOp",EDGE,"E14.22.20.0"),sQuery(id+"F0.wireOp",EDGE,"E14.26.20.0"),sQuery(id+"F0.wireOp",EDGE,"E14.29.20.0"),sQuery(id+"F0.wireOp",EDGE,"E14.1.21.0"),sQuery(id+"F0.wireOp",EDGE,"E14.4.21.0"),sQuery(id+"F0.wireOp",EDGE,"E14.7.21.0"),sQuery(id+"F0.wireOp",EDGE,"E14.11.21.0"),sQuery(id+"F0.wireOp",EDGE,"E14.15.21.0"),sQuery(id+"F0.wireOp",EDGE,"E14.18.21.0"),sQuery(id+"F0.wireOp",EDGE,"E14.22.21.0"),sQuery(id+"F0.wireOp",EDGE,"E14.26.21.0"),sQuery(id+"F0.wireOp",EDGE,"E14.29.21.0"),sQuery(id+"F0.wireOp",EDGE,"E14.1.22.0"),sQuery(id+"F0.wireOp",EDGE,"E14.4.22.0"),sQuery(id+"F0.wireOp",EDGE,"E14.7.22.0"),sQuery(id+"F0.wireOp",EDGE,"E14.11.22.0"),sQuery(id+"F0.wireOp",EDGE,"E14.15.22.0"),sQuery(id+"F0.wireOp",EDGE,"E14.18.22.0"),sQuery(id+"F0.wireOp",EDGE,"E14.22.22.0"),sQuery(id+"F0.wireOp",EDGE,"E14.26.22.0"),sQuery(id+"F0.wireOp",EDGE,"E14.29.22.0"),sQuery(id+"F0.wireOp",EDGE,"E14.1.23.0"),sQuery(id+"F0.wireOp",EDGE,"E14.4.23.0"),sQuery(id+"F0.wireOp",EDGE,"E14.7.23.0"),sQuery(id+"F0.wireOp",EDGE,"E14.11.23.0"),sQuery(id+"F0.wireOp",EDGE,"E14.15.23.0"),sQuery(id+"F0.wireOp",EDGE,"E14.18.23.0"),sQuery(id+"F0.wireOp",EDGE,"E14.22.23.0"),sQuery(id+"F0.wireOp",EDGE,"E14.26.23.0"),sQuery(id+"F0.wireOp",EDGE,"E14.29.23.0"),sQuery(id+"F0.wireOp",EDGE,"E14.1.24.0"),sQuery(id+"F0.wireOp",EDGE,"E14.4.24.0"),sQuery(id+"F0.wireOp",EDGE,"E14.7.24.0"),sQuery(id+"F0.wireOp",EDGE,"E14.11.24.0"),sQuery(id+"F0.wireOp",EDGE,"E14.15.24.0"),sQuery(id+"F0.wireOp",EDGE,"E14.18.24.0"),sQuery(id+"F0.wireOp",EDGE,"E14.22.24.0"),sQuery(id+"F0.wireOp",EDGE,"E14.26.24.0"),sQuery(id+"F0.wireOp",EDGE,"E14.29.24.0"),sQuery(id+"F0.wireOp",EDGE,"E14.1.25.0"),sQuery(id+"F0.wireOp",EDGE,"E14.4.25.0"),sQuery(id+"F0.wireOp",EDGE,"E14.7.25.0"),sQuery(id+"F0.wireOp",EDGE,"E14.11.25.0"),sQuery(id+"F0.wireOp",EDGE,"E14.15.25.0"),sQuery(id+"F0.wireOp",EDGE,"E14.18.25.0"),sQuery(id+"F0.wireOp",EDGE,"E14.22.25.0"),sQuery(id+"F0.wireOp",EDGE,"E14.26.25.0"),sQuery(id+"F0.wireOp",EDGE,"E14.29.25.0"),sQuery(id+"F0.wireOp",EDGE,"E14.1.26.0"),sQuery(id+"F0.wireOp",EDGE,"E14.4.26.0"),sQuery(id+"F0.wireOp",EDGE,"E14.7.26.0"),sQuery(id+"F0.wireOp",EDGE,"E14.11.26.0"),sQuery(id+"F0.wireOp",EDGE,"E14.15.26.0"),sQuery(id+"F0.wireOp",EDGE,"E14.18.26.0"),sQuery(id+"F0.wireOp",EDGE,"E14.22.26.0"),sQuery(id+"F0.wireOp",EDGE,"E14.26.26.0"),sQuery(id+"F0.wireOp",EDGE,"E14.29.26.0"),sQuery(id+"F0.wireOp",EDGE,"E14.1.27.0"),sQuery(id+"F0.wireOp",EDGE,"E14.4.27.0"),sQuery(id+"F0.wireOp",EDGE,"E14.7.27.0"),sQuery(id+"F0.wireOp",EDGE,"E14.11.27.0"),sQuery(id+"F0.wireOp",EDGE,"E14.15.27.0"),sQuery(id+"F0.wireOp",EDGE,"E14.18.27.0"),sQuery(id+"F0.wireOp",EDGE,"E14.22.27.0"),sQuery(id+"F0.wireOp",EDGE,"E14.26.27.0"),sQuery(id+"F0.wireOp",EDGE,"E14.29.27.0"),sQuery(id+"F0.wireOp",EDGE,"E14.1.28.0"),sQuery(id+"F0.wireOp",EDGE,"E14.4.28.0"),sQuery(id+"F0.wireOp",EDGE,"E14.7.28.0"),sQuery(id+"F0.wireOp",EDGE,"E14.11.28.0"),sQuery(id+"F0.wireOp",EDGE,"E14.15.28.0"),sQuery(id+"F0.wireOp",EDGE,"E14.18.28.0"),sQuery(id+"F0.wireOp",EDGE,"E14.22.28.0"),sQuery(id+"F0.wireOp",EDGE,"E14.26.28.0"),sQuery(id+"F0.wireOp",EDGE,"E14.29.28.0"),sQuery(id+"F0.wireOp",EDGE,"E14.1.29.0"),sQuery(id+"F0.wireOp",EDGE,"E14.4.29.0"),sQuery(id+"F0.wireOp",EDGE,"E14.7.29.0"),sQuery(id+"F0.wireOp",EDGE,"E14.11.29.0"),sQuery(id+"F0.wireOp",EDGE,"E14.15.29.0"),sQuery(id+"F0.wireOp",EDGE,"E14.18.29.0"),sQuery(id+"F0.wireOp",EDGE,"E14.22.29.0"),sQuery(id+"F0.wireOp",EDGE,"E14.26.29.0"),sQuery(id+"F0.wireOp",EDGE,"E14.29.29.0"),sQuery(id+"F0.wireOp",EDGE,"E14.1.30.0"),sQuery(id+"F0.wireOp",EDGE,"E14.4.30.0"),sQuery(id+"F0.wireOp",EDGE,"E14.7.30.0"),sQuery(id+"F0.wireOp",EDGE,"E14.11.30.0"),sQuery(id+"F0.wireOp",EDGE,"E14.15.30.0"),sQuery(id+"F0.wireOp",EDGE,"E14.18.30.0"),sQuery(id+"F0.wireOp",EDGE,"E14.22.30.0"),sQuery(id+"F0.wireOp",EDGE,"E14.26.30.0"),sQuery(id+"F0.wireOp",EDGE,"E14.29.30.0"),sQuery(id+"F0.wireOp",EDGE,"E14.1.31.0"),sQuery(id+"F0.wireOp",EDGE,"E14.4.31.0"),sQuery(id+"F0.wireOp",EDGE,"E14.7.31.0"),sQuery(id+"F0.wireOp",EDGE,"E14.11.31.0"),sQuery(id+"F0.wireOp",EDGE,"E14.15.31.0"),sQuery(id+"F0.wireOp",EDGE,"E14.18.31.0"),sQuery(id+"F0.wireOp",EDGE,"E14.22.31.0"),sQuery(id+"F0.wireOp",EDGE,"E14.26.31.0"),sQuery(id+"F0.wireOp",EDGE,"E14.29.31.0"),sQuery(id+"F0.wireOp",EDGE,"E14.1.32.0"),sQuery(id+"F0.wireOp",EDGE,"E14.4.32.0"),sQuery(id+"F0.wireOp",EDGE,"E14.7.32.0"),sQuery(id+"F0.wireOp",EDGE,"E14.11.32.0"),sQuery(id+"F0.wireOp",EDGE,"E14.15.32.0"),sQuery(id+"F0.wireOp",EDGE,"E14.18.32.0"),sQuery(id+"F0.wireOp",EDGE,"E14.22.32.0"),sQuery(id+"F0.wireOp",EDGE,"E14.26.32.0"),sQuery(id+"F0.wireOp",EDGE,"E14.29.32.0"),sQuery(id+"F0.wireOp",EDGE,"E14.1.33.0"),sQuery(id+"F0.wireOp",EDGE,"E14.4.33.0"),sQuery(id+"F0.wireOp",EDGE,"E14.7.33.0"),sQuery(id+"F0.wireOp",EDGE,"E14.11.33.0"),sQuery(id+"F0.wireOp",EDGE,"E14.15.33.0"),sQuery(id+"F0.wireOp",EDGE,"E14.18.33.0"),sQuery(id+"F0.wireOp",EDGE,"E14.22.33.0"),sQuery(id+"F0.wireOp",EDGE,"E14.26.33.0"),sQuery(id+"F0.wireOp",EDGE,"E14.29.33.0"),sQuery(id+"F0.wireOp",EDGE,"E14.1.34.0"),sQuery(id+"F0.wireOp",EDGE,"E14.4.34.0"),sQuery(id+"F0.wireOp",EDGE,"E14.7.34.0"),sQuery(id+"F0.wireOp",EDGE,"E14.11.34.0"),sQuery(id+"F0.wireOp",EDGE,"E14.15.34.0"),sQuery(id+"F0.wireOp",EDGE,"E14.18.34.0"),sQuery(id+"F0.wireOp",EDGE,"E14.22.34.0"),sQuery(id+"F0.wireOp",EDGE,"E14.26.34.0"),sQuery(id+"F0.wireOp",EDGE,"E14.29.34.0"),sQuery(id+"F0.wireOp",EDGE,"E14.1.35.0"),sQuery(id+"F0.wireOp",EDGE,"E14.4.35.0"),sQuery(id+"F0.wireOp",EDGE,"E14.7.35.0"),sQuery(id+"F0.wireOp",EDGE,"E14.11.35.0"),sQuery(id+"F0.wireOp",EDGE,"E14.15.35.0"),sQuery(id+"F0.wireOp",EDGE,"E14.18.35.0"),sQuery(id+"F0.wireOp",EDGE,"E14.22.35.0"),sQuery(id+"F0.wireOp",EDGE,"E14.26.35.0"),sQuery(id+"F0.wireOp",EDGE,"E14.29.35.0"),sQuery(id+"F0.wireOp",EDGE,"E14.1.36.0"),sQuery(id+"F0.wireOp",EDGE,"E14.4.36.0"),sQuery(id+"F0.wireOp",EDGE,"E14.7.36.0"),sQuery(id+"F0.wireOp",EDGE,"E14.11.36.0"),sQuery(id+"F0.wireOp",EDGE,"E14.15.36.0"),sQuery(id+"F0.wireOp",EDGE,"E14.18.36.0"),sQuery(id+"F0.wireOp",EDGE,"E14.22.36.0"),sQuery(id+"F0.wireOp",EDGE,"E14.26.36.0"),sQuery(id+"F0.wireOp",EDGE,"E14.29.36.0"),sQuery(id+"F0.wireOp",EDGE,"E14.1.37.0"),sQuery(id+"F0.wireOp",EDGE,"E14.4.37.0"),sQuery(id+"F0.wireOp",EDGE,"E14.7.37.0"),sQuery(id+"F0.wireOp",EDGE,"E14.11.37.0"),sQuery(id+"F0.wireOp",EDGE,"E14.15.37.0"),sQuery(id+"F0.wireOp",EDGE,"E14.18.37.0"),sQuery(id+"F0.wireOp",EDGE,"E14.22.37.0"),sQuery(id+"F0.wireOp",EDGE,"E14.26.37.0"),sQuery(id+"F0.wireOp",EDGE,"E14.29.37.0"),sQuery(id+"F0.wireOp",EDGE,"E14.1.38.0"),sQuery(id+"F0.wireOp",EDGE,"E14.4.38.0"),sQuery(id+"F0.wireOp",EDGE,"E14.7.38.0"),sQuery(id+"F0.wireOp",EDGE,"E14.11.38.0"),sQuery(id+"F0.wireOp",EDGE,"E14.15.38.0"),sQuery(id+"F0.wireOp",EDGE,"E14.18.38.0"),sQuery(id+"F0.wireOp",EDGE,"E14.22.38.0"),sQuery(id+"F0.wireOp",EDGE,"E14.26.38.0"),sQuery(id+"F0.wireOp",EDGE,"E14.29.38.0"),sQuery(id+"F0.wireOp",EDGE,"E14.1.39.0"),sQuery(id+"F0.wireOp",EDGE,"E14.4.39.0"),sQuery(id+"F0.wireOp",EDGE,"E14.7.39.0"),sQuery(id+"F0.wireOp",EDGE,"E14.11.39.0"),sQuery(id+"F0.wireOp",EDGE,"E14.15.39.0"),sQuery(id+"F0.wireOp",EDGE,"E14.18.39.0"),sQuery(id+"F0.wireOp",EDGE,"E14.22.39.0"),sQuery(id+"F0.wireOp",EDGE,"E14.26.39.0"),sQuery(id+"F0.wireOp",EDGE,"E14.29.39.0"),sQuery(id+"F0.wireOp",EDGE,"E14.1.40.0"),sQuery(id+"F0.wireOp",EDGE,"E14.4.40.0"),sQuery(id+"F0.wireOp",EDGE,"E14.7.40.0"),sQuery(id+"F0.wireOp",EDGE,"E14.11.40.0"),sQuery(id+"F0.wireOp",EDGE,"E14.15.40.0"),sQuery(id+"F0.wireOp",EDGE,"E14.18.40.0"),sQuery(id+"F0.wireOp",EDGE,"E14.22.40.0"),sQuery(id+"F0.wireOp",EDGE,"E14.26.40.0"),sQuery(id+"F0.wireOp",EDGE,"E14.29.40.0"),sQuery(id+"F0.wireOp",EDGE,"E14.1.41.0"),sQuery(id+"F0.wireOp",EDGE,"E14.4.41.0"),sQuery(id+"F0.wireOp",EDGE,"E14.7.41.0"),sQuery(id+"F0.wireOp",EDGE,"E14.11.41.0"),sQuery(id+"F0.wireOp",EDGE,"E14.15.41.0"),sQuery(id+"F0.wireOp",EDGE,"E14.18.41.0"),sQuery(id+"F0.wireOp",EDGE,"E14.22.41.0"),sQuery(id+"F0.wireOp",EDGE,"E14.26.41.0"),sQuery(id+"F0.wireOp",EDGE,"E14.29.41.0"),sQuery(id+"F0.wireOp",EDGE,"E14.1.42.0"),sQuery(id+"F0.wireOp",EDGE,"E14.4.42.0"),sQuery(id+"F0.wireOp",EDGE,"E14.7.42.0"),sQuery(id+"F0.wireOp",EDGE,"E14.11.42.0"),sQuery(id+"F0.wireOp",EDGE,"E14.15.42.0"),sQuery(id+"F0.wireOp",EDGE,"E14.18.42.0"),sQuery(id+"F0.wireOp",EDGE,"E14.22.42.0"),sQuery(id+"F0.wireOp",EDGE,"E14.26.42.0"),sQuery(id+"F0.wireOp",EDGE,"E14.29.42.0"),sQuery(id+"F0.wireOp",EDGE,"E14.1.43.0"),sQuery(id+"F0.wireOp",EDGE,"E14.4.43.0"),sQuery(id+"F0.wireOp",EDGE,"E14.7.43.0"),sQuery(id+"F0.wireOp",EDGE,"E14.11.43.0"),sQuery(id+"F0.wireOp",EDGE,"E14.15.43.0"),sQuery(id+"F0.wireOp",EDGE,"E14.18.43.0"),sQuery(id+"F0.wireOp",EDGE,"E14.22.43.0"),sQuery(id+"F0.wireOp",EDGE,"E14.26.43.0"),sQuery(id+"F0.wireOp",EDGE,"E14.29.43.0"),sQuery(id+"F0.wireOp",EDGE,"E14.1.44.0"),sQuery(id+"F0.wireOp",EDGE,"E14.4.44.0"),sQuery(id+"F0.wireOp",EDGE,"E14.7.44.0"),sQuery(id+"F0.wireOp",EDGE,"E14.11.44.0"),sQuery(id+"F0.wireOp",EDGE,"E14.15.44.0"),sQuery(id+"F0.wireOp",EDGE,"E14.18.44.0"),sQuery(id+"F0.wireOp",EDGE,"E14.22.44.0"),sQuery(id+"F0.wireOp",EDGE,"E14.26.44.0"),sQuery(id+"F0.wireOp",EDGE,"E14.29.44.0"),sQuery(id+"F0.wireOp",EDGE,"E14.1.45.0"),sQuery(id+"F0.wireOp",EDGE,"E14.4.45.0"),sQuery(id+"F0.wireOp",EDGE,"E14.7.45.0"),sQuery(id+"F0.wireOp",EDGE,"E14.11.45.0"),sQuery(id+"F0.wireOp",EDGE,"E14.15.45.0"),sQuery(id+"F0.wireOp",EDGE,"E14.18.45.0"),sQuery(id+"F0.wireOp",EDGE,"E14.22.45.0"),sQuery(id+"F0.wireOp",EDGE,"E14.26.45.0"),sQuery(id+"F0.wireOp",EDGE,"E14.29.45.0"),sQuery(id+"F0.wireOp",EDGE,"E14.1.46.0"),sQuery(id+"F0.wireOp",EDGE,"E14.4.46.0"),sQuery(id+"F0.wireOp",EDGE,"E14.7.46.0"),sQuery(id+"F0.wireOp",EDGE,"E14.11.46.0"),sQuery(id+"F0.wireOp",EDGE,"E14.15.46.0"),sQuery(id+"F0.wireOp",EDGE,"E14.18.46.0"),sQuery(id+"F0.wireOp",EDGE,"E14.22.46.0"),sQuery(id+"F0.wireOp",EDGE,"E14.26.46.0"),sQuery(id+"F0.wireOp",EDGE,"E14.29.46.0"),sQuery(id+"F0.wireOp",EDGE,"E14.1.47.0"),sQuery(id+"F0.wireOp",EDGE,"E14.4.47.0"),sQuery(id+"F0.wireOp",EDGE,"E14.7.47.0"),sQuery(id+"F0.wireOp",EDGE,"E14.11.47.0"),sQuery(id+"F0.wireOp",EDGE,"E14.15.47.0"),sQuery(id+"F0.wireOp",EDGE,"E14.18.47.0"),sQuery(id+"F0.wireOp",EDGE,"E14.22.47.0"),sQuery(id+"F0.wireOp",EDGE,"E14.26.47.0"),sQuery(id+"F0.wireOp",EDGE,"E14.29.47.0"),sQuery(id+"F0.wireOp",EDGE,"E14.1.48.0"),sQuery(id+"F0.wireOp",EDGE,"E14.4.48.0"),sQuery(id+"F0.wireOp",EDGE,"E14.7.48.0"),sQuery(id+"F0.wireOp",EDGE,"E14.11.48.0"),sQuery(id+"F0.wireOp",EDGE,"E14.15.48.0"),sQuery(id+"F0.wireOp",EDGE,"E14.18.48.0"),sQuery(id+"F0.wireOp",EDGE,"E14.22.48.0"),sQuery(id+"F0.wireOp",EDGE,"E14.26.48.0"),sQuery(id+"F0.wireOp",EDGE,"E14.29.48.0"),sQuery(id+"F0.wireOp",EDGE,"E14.1.49.0"),sQuery(id+"F0.wireOp",EDGE,"E14.4.49.0"),sQuery(id+"F0.wireOp",EDGE,"E14.7.49.0"),sQuery(id+"F0.wireOp",EDGE,"E14.11.49.0"),sQuery(id+"F0.wireOp",EDGE,"E14.15.49.0"),sQuery(id+"F0.wireOp",EDGE,"E14.18.49.0"),sQuery(id+"F0.wireOp",EDGE,"E14.22.49.0"),sQuery(id+"F0.wireOp",EDGE,"E14.26.49.0"),sQuery(id+"F0.wireOp",EDGE,"E14.29.49.0"),sQuery(id+"F0.wireOp",EDGE,"E14.1.50.0"),sQuery(id+"F0.wireOp",EDGE,"E14.4.50.0"),sQuery(id+"F0.wireOp",EDGE,"E14.7.50.0"),sQuery(id+"F0.wireOp",EDGE,"E14.11.50.0"),sQuery(id+"F0.wireOp",EDGE,"E14.15.50.0"),sQuery(id+"F0.wireOp",EDGE,"E14.18.50.0"),sQuery(id+"F0.wireOp",EDGE,"E14.22.50.0"),sQuery(id+"F0.wireOp",EDGE,"E14.26.50.0"),sQuery(id+"F0.wireOp",EDGE,"E14.29.50.0"),sQuery(id+"F0.wireOp",EDGE,"E14.1.51.0"),sQuery(id+"F0.wireOp",EDGE,"E14.4.51.0"),sQuery(id+"F0.wireOp",EDGE,"E14.7.51.0"),sQuery(id+"F0.wireOp",EDGE,"E14.11.51.0"),sQuery(id+"F0.wireOp",EDGE,"E14.15.51.0"),sQuery(id+"F0.wireOp",EDGE,"E14.18.51.0"),sQuery(id+"F0.wireOp",EDGE,"E14.22.51.0"),sQuery(id+"F0.wireOp",EDGE,"E14.26.51.0"),sQuery(id+"F0.wireOp",EDGE,"E14.29.51.0"),sQuery(id+"F0.wireOp",EDGE,"E14.1.52.0"),sQuery(id+"F0.wireOp",EDGE,"E14.4.52.0"),sQuery(id+"F0.wireOp",EDGE,"E14.7.52.0"),sQuery(id+"F0.wireOp",EDGE,"E14.11.52.0"),sQuery(id+"F0.wireOp",EDGE,"E14.15.52.0"),sQuery(id+"F0.wireOp",EDGE,"E14.18.52.0"),sQuery(id+"F0.wireOp",EDGE,"E14.22.52.0"),sQuery(id+"F0.wireOp",EDGE,"E14.26.52.0"),sQuery(id+"F0.wireOp",EDGE,"E14.29.52.0"),sQuery(id+"F0.wireOp",EDGE,"E14.1.53.0"),sQuery(id+"F0.wireOp",EDGE,"E14.4.53.0"),sQuery(id+"F0.wireOp",EDGE,"E14.7.53.0"),sQuery(id+"F0.wireOp",EDGE,"E14.11.53.0"),sQuery(id+"F0.wireOp",EDGE,"E14.15.53.0"),sQuery(id+"F0.wireOp",EDGE,"E14.18.53.0"),sQuery(id+"F0.wireOp",EDGE,"E14.22.53.0"),sQuery(id+"F0.wireOp",EDGE,"E14.26.53.0"),sQuery(id+"F0.wireOp",EDGE,"E14.29.53.0"),sQuery(id+"F0.wireOp",EDGE,"E14.1.54.0"),sQuery(id+"F0.wireOp",EDGE,"E14.4.54.0"),sQuery(id+"F0.wireOp",EDGE,"E14.7.54.0"),sQuery(id+"F0.wireOp",EDGE,"E14.11.54.0"),sQuery(id+"F0.wireOp",EDGE,"E14.15.54.0"),sQuery(id+"F0.wireOp",EDGE,"E14.18.54.0"),sQuery(id+"F0.wireOp",EDGE,"E14.22.54.0"),sQuery(id+"F0.wireOp",EDGE,"E14.26.54.0"),sQuery(id+"F0.wireOp",EDGE,"E14.29.54.0"),sQuery(id+"F0.wireOp",EDGE,"E14.1.55.0"),sQuery(id+"F0.wireOp",EDGE,"E14.4.55.0"),sQuery(id+"F0.wireOp",EDGE,"E14.7.55.0"),sQuery(id+"F0.wireOp",EDGE,"E14.11.55.0"),sQuery(id+"F0.wireOp",EDGE,"E14.15.55.0"),sQuery(id+"F0.wireOp",EDGE,"E14.18.55.0"),sQuery(id+"F0.wireOp",EDGE,"E14.22.55.0"),sQuery(id+"F0.wireOp",EDGE,"E14.26.55.0"),sQuery(id+"F0.wireOp",EDGE,"E14.29.55.0"),sQuery(id+"F0.wireOp",EDGE,"E14.1.56.0"),sQuery(id+"F0.wireOp",EDGE,"E14.4.56.0"),sQuery(id+"F0.wireOp",EDGE,"E14.7.56.0"),sQuery(id+"F0.wireOp",EDGE,"E14.11.56.0"),sQuery(id+"F0.wireOp",EDGE,"E14.15.56.0"),sQuery(id+"F0.wireOp",EDGE,"E14.18.56.0"),sQuery(id+"F0.wireOp",EDGE,"E14.22.56.0"),sQuery(id+"F0.wireOp",EDGE,"E14.26.56.0"),sQuery(id+"F0.wireOp",EDGE,"E14.29.56.0"),sQuery(id+"F0.wireOp",EDGE,"E14.1.57.0"),sQuery(id+"F0.wireOp",EDGE,"E14.4.57.0"),sQuery(id+"F0.wireOp",EDGE,"E14.7.57.0"),sQuery(id+"F0.wireOp",EDGE,"E14.11.57.0"),sQuery(id+"F0.wireOp",EDGE,"E14.15.57.0"),sQuery(id+"F0.wireOp",EDGE,"E14.18.57.0"),sQuery(id+"F0.wireOp",EDGE,"E14.22.57.0"),sQuery(id+"F0.wireOp",EDGE,"E14.26.57.0"),sQuery(id+"F0.wireOp",EDGE,"E14.29.57.0"),sQuery(id+"F0.wireOp",EDGE,"E14.1.58.0"),sQuery(id+"F0.wireOp",EDGE,"E14.4.58.0"),sQuery(id+"F0.wireOp",EDGE,"E14.7.58.0"),sQuery(id+"F0.wireOp",EDGE,"E14.11.58.0"),sQuery(id+"F0.wireOp",EDGE,"E14.15.58.0"),sQuery(id+"F0.wireOp",EDGE,"E14.18.58.0"),sQuery(id+"F0.wireOp",EDGE,"E14.22.58.0"),sQuery(id+"F0.wireOp",EDGE,"E14.26.58.0"),sQuery(id+"F0.wireOp",EDGE,"E14.29.58.0"),sQuery(id+"F0.wireOp",EDGE,"E14.1.59.0"),sQuery(id+"F0.wireOp",EDGE,"E14.4.59.0"),sQuery(id+"F0.wireOp",EDGE,"E14.7.59.0"),sQuery(id+"F0.wireOp",EDGE,"E14.11.59.0"),sQuery(id+"F0.wireOp",EDGE,"E14.15.59.0"),sQuery(id+"F0.wireOp",EDGE,"E14.18.59.0"),sQuery(id+"F0.wireOp",EDGE,"E14.22.59.0"),sQuery(id+"F0.wireOp",EDGE,"E14.26.59.0"),sQuery(id+"F0.wireOp",EDGE,"E14.29.59.0"),sQuery(id+"F0.wireOp",EDGE,"E14.1.60.0"),sQuery(id+"F0.wireOp",EDGE,"E14.4.60.0"),sQuery(id+"F0.wireOp",EDGE,"E14.7.60.0"),sQuery(id+"F0.wireOp",EDGE,"E14.11.60.0"),sQuery(id+"F0.wireOp",EDGE,"E14.15.60.0"),sQuery(id+"F0.wireOp",EDGE,"E14.18.60.0"),sQuery(id+"F0.wireOp",EDGE,"E14.22.60.0"),sQuery(id+"F0.wireOp",EDGE,"E14.26.60.0"),sQuery(id+"F0.wireOp",EDGE,"E14.29.60.0"),sQuery(id+"F0.wireOp",EDGE,"E14.1.61.0"),sQuery(id+"F0.wireOp",EDGE,"E14.4.61.0"),sQuery(id+"F0.wireOp",EDGE,"E14.7.61.0"),sQuery(id+"F0.wireOp",EDGE,"E14.11.61.0"),sQuery(id+"F0.wireOp",EDGE,"E14.15.61.0"),sQuery(id+"F0.wireOp",EDGE,"E14.18.61.0"),sQuery(id+"F0.wireOp",EDGE,"E14.22.61.0"),sQuery(id+"F0.wireOp",EDGE,"E14.26.61.0"),sQuery(id+"F0.wireOp",EDGE,"E14.29.61.0"),sQuery(id+"F0.wireOp",EDGE,"E14.1.62.0"),sQuery(id+"F0.wireOp",EDGE,"E14.4.62.0"),sQuery(id+"F0.wireOp",EDGE,"E14.7.62.0"),sQuery(id+"F0.wireOp",EDGE,"E14.11.62.0"),sQuery(id+"F0.wireOp",EDGE,"E14.15.62.0"),sQuery(id+"F0.wireOp",EDGE,"E14.18.62.0"),sQuery(id+"F0.wireOp",EDGE,"E14.22.62.0"),sQuery(id+"F0.wireOp",EDGE,"E14.26.62.0"),sQuery(id+"F0.wireOp",EDGE,"E14.29.62.0"),sQuery(id+"F0.wireOp",EDGE,"E14.1.63.0"),sQuery(id+"F0.wireOp",EDGE,"E14.4.63.0"),sQuery(id+"F0.wireOp",EDGE,"E14.7.63.0"),sQuery(id+"F0.wireOp",EDGE,"E14.11.63.0"),sQuery(id+"F0.wireOp",EDGE,"E14.15.63.0"),sQuery(id+"F0.wireOp",EDGE,"E14.18.63.0"),sQuery(id+"F0.wireOp",EDGE,"E14.22.63.0"),sQuery(id+"F0.wireOp",EDGE,"E14.26.63.0"),sQuery(id+"F0.wireOp",EDGE,"E14.29.63.0"),sQuery(id+"F0.wireOp",EDGE,"E14.1.64.0"),sQuery(id+"F0.wireOp",EDGE,"E14.4.64.0"),sQuery(id+"F0.wireOp",EDGE,"E14.7.64.0"),sQuery(id+"F0.wireOp",EDGE,"E14.11.64.0"),sQuery(id+"F0.wireOp",EDGE,"E14.15.64.0"),sQuery(id+"F0.wireOp",EDGE,"E14.18.64.0"),sQuery(id+"F0.wireOp",EDGE,"E14.22.64.0"),sQuery(id+"F0.wireOp",EDGE,"E14.26.64.0"),sQuery(id+"F0.wireOp",EDGE,"E14.29.64.0"),sQuery(id+"F0.wireOp",EDGE,"E14.1.65.0"),sQuery(id+"F0.wireOp",EDGE,"E14.4.65.0"),sQuery(id+"F0.wireOp",EDGE,"E14.7.65.0"),sQuery(id+"F0.wireOp",EDGE,"E14.11.65.0"),sQuery(id+"F0.wireOp",EDGE,"E14.15.65.0"),sQuery(id+"F0.wireOp",EDGE,"E14.18.65.0"),sQuery(id+"F0.wireOp",EDGE,"E14.22.65.0"),sQuery(id+"F0.wireOp",EDGE,"E14.26.65.0"),sQuery(id+"F0.wireOp",EDGE,"E14.29.65.0"),sQuery(id+"F0.wireOp",EDGE,"E14.1.66.0"),sQuery(id+"F0.wireOp",EDGE,"E14.4.66.0"),sQuery(id+"F0.wireOp",EDGE,"E14.7.66.0"),sQuery(id+"F0.wireOp",EDGE,"E14.11.66.0"),sQuery(id+"F0.wireOp",EDGE,"E14.15.66.0"),sQuery(id+"F0.wireOp",EDGE,"E14.18.66.0"),sQuery(id+"F0.wireOp",EDGE,"E14.22.66.0"),sQuery(id+"F0.wireOp",EDGE,"E14.26.66.0"),sQuery(id+"F0.wireOp",EDGE,"E14.29.66.0"),sQuery(id+"F0.wireOp",EDGE,"E14.1.67.0"),sQuery(id+"F0.wireOp",EDGE,"E14.4.67.0"),sQuery(id+"F0.wireOp",EDGE,"E14.7.67.0"),sQuery(id+"F0.wireOp",EDGE,"E14.11.67.0"),sQuery(id+"F0.wireOp",EDGE,"E14.15.67.0"),sQuery(id+"F0.wireOp",EDGE,"E14.18.67.0"),sQuery(id+"F0.wireOp",EDGE,"E14.22.67.0"),sQuery(id+"F0.wireOp",EDGE,"E14.26.67.0"),sQuery(id+"F0.wireOp",EDGE,"E14.29.67.0"),sQuery(id+"F0.wireOp",EDGE,"E14.1.68.0"),sQuery(id+"F0.wireOp",EDGE,"E14.4.68.0"),sQuery(id+"F0.wireOp",EDGE,"E14.7.68.0"),sQuery(id+"F0.wireOp",EDGE,"E14.11.68.0"),sQuery(id+"F0.wireOp",EDGE,"E14.15.68.0"),sQuery(id+"F0.wireOp",EDGE,"E14.18.68.0"),sQuery(id+"F0.wireOp",EDGE,"E14.22.68.0"),sQuery(id+"F0.wireOp",EDGE,"E14.26.68.0"),sQuery(id+"F0.wireOp",EDGE,"E14.29.68.0"),sQuery(id+"F0.wireOp",EDGE,"E14.1.69.0"),sQuery(id+"F0.wireOp",EDGE,"E14.4.69.0"),sQuery(id+"F0.wireOp",EDGE,"E14.7.69.0"),sQuery(id+"F0.wireOp",EDGE,"E14.11.69.0"),sQuery(id+"F0.wireOp",EDGE,"E14.15.69.0"),sQuery(id+"F0.wireOp",EDGE,"E14.18.69.0"),sQuery(id+"F0.wireOp",EDGE,"E14.22.69.0"),sQuery(id+"F0.wireOp",EDGE,"E14.26.69.0"),sQuery(id+"F0.wireOp",EDGE,"E14.29.69.0"),sQuery(id+"F0.wireOp",EDGE,"E14.1.70.0"),sQuery(id+"F0.wireOp",EDGE,"E14.4.70.0"),sQuery(id+"F0.wireOp",EDGE,"E14.7.70.0"),sQuery(id+"F0.wireOp",EDGE,"E14.11.70.0"),sQuery(id+"F0.wireOp",EDGE,"E14.15.70.0"),sQuery(id+"F0.wireOp",EDGE,"E14.18.70.0"),sQuery(id+"F0.wireOp",EDGE,"E14.22.70.0"),sQuery(id+"F0.wireOp",EDGE,"E14.26.70.0"),sQuery(id+"F0.wireOp",EDGE,"E14.29.70.0"),sQuery(id+"F0.wireOp",EDGE,"E14.1.71.0"),sQuery(id+"F0.wireOp",EDGE,"E14.4.71.0"),sQuery(id+"F0.wireOp",EDGE,"E14.7.71.0"),sQuery(id+"F0.wireOp",EDGE,"E14.11.71.0"),sQuery(id+"F0.wireOp",EDGE,"E14.15.71.0"),sQuery(id+"F0.wireOp",EDGE,"E14.18.71.0"),sQuery(id+"F0.wireOp",EDGE,"E14.22.71.0"),sQuery(id+"F0.wireOp",EDGE,"E14.26.71.0"),sQuery(id+"F0.wireOp",EDGE,"E14.29.71.0"),sQuery(id+"F0.wireOp",EDGE,"E15.trimOffspring"),sQuery(id+"F0.wireOp",EDGE,"E16.trimOffspring"),sQuery(id+"F0.wireOp",EDGE,"E17.trimOffspring"),sQuery(id+"F0.wireOp",EDGE,"E18.trimOffspring"),sQuery(id+"F0.wireOp",EDGE,"E19.trimOffspring"),sQuery(id+"F0.wireOp",EDGE,"E20.trimOffspring"),sQuery(id+"F0.wireOp",EDGE,"E21.trimOffspring"),sQuery(id+"F0.wireOp",EDGE,"E22.trimOffspring"),sQuery(id+"F0.wireOp",EDGE,"E23.trimOffspring"),sQuery(id+"F0.wireOp",EDGE,"E24.trimOffspring"),sQuery(id+"F0.wireOp",EDGE,"E25.trimOffspring"),sQuery(id+"F0.wireOp",EDGE,"E26.trimOffspring"),sQuery(id+"F0.wireOp",EDGE,"E27.trimOffspring"),sQuery(id+"F0.wireOp",EDGE,"E28.trimOffspring"),sQuery(id+"F0.wireOp",EDGE,"E29.trimOffspring"),sQuery(id+"F0.wireOp",EDGE,"E30.trimOffspring"),sQuery(id+"F0.wireOp",EDGE,"E31.trimOffspring"),sQuery(id+"F0.wireOp",EDGE,"E32.trimOffspring"),sQuery(id+"F0.wireOp",EDGE,"E33.trimOffspring"),sQuery(id+"F0.wireOp",EDGE,"E34.trimOffspring"),sQuery(id+"F0.wireOp",EDGE,"E35.trimOffspring"),sQuery(id+"F0.wireOp",EDGE,"E36.trimOffspring"),sQuery(id+"F0.wireOp",EDGE,"E37.trimOffspring"),sQuery(id+"F0.wireOp",EDGE,"E38.trimOffspring"),sQuery(id+"F0.wireOp",EDGE,"E39.trimOffspring"),sQuery(id+"F0.wireOp",EDGE,"E40.trimOffspring"),sQuery(id+"F0.wireOp",EDGE,"E41.trimOffspring"),sQuery(id+"F0.wireOp",EDGE,"E42.trimOffspring"),sQuery(id+"F0.wireOp",EDGE,"E43.trimOffspring"),sQuery(id+"F0.wireOp",EDGE,"E44.trimOffspring"),sQuery(id+"F0.wireOp",EDGE,"E45.trimOffspring"),sQuery(id+"F0.wireOp",EDGE,"E46.trimOffspring"),sQuery(id+"F0.wireOp",EDGE,"E47.trimOffspring"),sQuery(id+"F0.wireOp",EDGE,"E48.trimOffspring"),sQuery(id+"F0.wireOp",EDGE,"E49.trimOffspring"),sQuery(id+"F0.wireOp",EDGE,"E50.trimOffspring"),sQuery(id+"F0.wireOp",EDGE,"E51.trimOffspring"),sQuery(id+"F0.wireOp",EDGE,"E52.trimOffspring"),sQuery(id+"F0.wireOp",EDGE,"E53.trimOffspring"),sQuery(id+"F0.wireOp",EDGE,"E54.trimOffspring"),sQuery(id+"F0.wireOp",EDGE,"E55.trimOffspring"),sQuery(id+"F0.wireOp",EDGE,"E56.trimOffspring"),sQuery(id+"F0.wireOp",EDGE,"E57.trimOffspring"),sQuery(id+"F0.wireOp",EDGE,"E58.trimOffspring"),sQuery(id+"F0.wireOp",EDGE,"E59.trimOffspring"),sQuery(id+"F0.wireOp",EDGE,"E60.trimOffspring"),sQuery(id+"F0.wireOp",EDGE,"E61.trimOffspring"),sQuery(id+"F0.wireOp",EDGE,"E62.trimOffspring"),sQuery(id+"F0.wireOp",EDGE,"E63.trimOffspring"),sQuery(id+"F0.wireOp",EDGE,"E64.trimOffspring"),sQuery(id+"F0.wireOp",EDGE,"E65.trimOffspring"),sQuery(id+"F0.wireOp",EDGE,"E66.trimOffspring"),sQuery(id+"F0.wireOp",EDGE,"E67.trimOffspring"),sQuery(id+"F0.wireOp",EDGE,"E68.trimOffspring"),sQuery(id+"F0.wireOp",EDGE,"E69.trimOffspring"),sQuery(id+"F0.wireOp",EDGE,"E70.trimOffspring"),sQuery(id+"F0.wireOp",EDGE,"E71.trimOffspring"),sQuery(id+"F0.wireOp",EDGE,"E72.trimOffspring"),sQuery(id+"F0.wireOp",EDGE,"E73.trimOffspring"),sQuery(id+"F0.wireOp",EDGE,"E74.trimOffspring"),sQuery(id+"F0.wireOp",EDGE,"E75.trimOffspring"),sQuery(id+"F0.wireOp",EDGE,"E76.trimOffspring"),sQuery(id+"F0.wireOp",EDGE,"E77.trimOffspring"),sQuery(id+"F0.wireOp",EDGE,"E78.trimOffspring"),sQuery(id+"F0.wireOp",EDGE,"E79.trimOffspring"),sQuery(id+"F0.wireOp",EDGE,"E80.trimOffspring"),sQuery(id+"F0.wireOp",EDGE,"E81.trimOffspring"),sQuery(id+"F0.wireOp",EDGE,"E82.trimOffspring"),sQuery(id+"F0.wireOp",EDGE,"E83.trimOffspring"),sQuery(id+"F0.wireOp",EDGE,"E84.trimOffspring"),sQuery(id+"F0.wireOp",EDGE,"E85.trimOffspring")])],"isStart":false});
            var sketch = newSketch(context, id + "F3", { "sketchPlane" : qUnion([Q0])});
            skCircle(sketch, "E86", {"center": v(0, 0) * mm, "radius": 6.35 * mm});
            skCircle(sketch, "E87", {"center": v(50.8, 0) * mm, "radius": 6.35 * mm});
            skCircle(sketch, "E88.1.0", {"center": v(-25.4, 44) * mm, "radius": 6.35 * mm});
            skCircle(sketch, "E88.2.0", {"center": v(-25.4, -44) * mm, "radius": 6.35 * mm});
            skSolve(sketch);
        }
        {
            var Q0;
            Q0 = qSketchRegion(id + "F3", true);
            var Q1;
            Q1=makeQuery(id+"F3.imprint","IMPRINT",FACE,{"disambiguationData":[TD([[makeQuery(id+"F3.imprint","IMPRINT",EDGE,{"derivedFrom":sQuery(id+"F3.wireOp",EDGE,"E86")}),1.0]])]});
            extrude(context, id + "F4", {"entities" : qUnion([Q0, Q1]), "operationType" : NewBodyOperationType.ADD, "depth" : 6.35 * mm});
        }
    });
